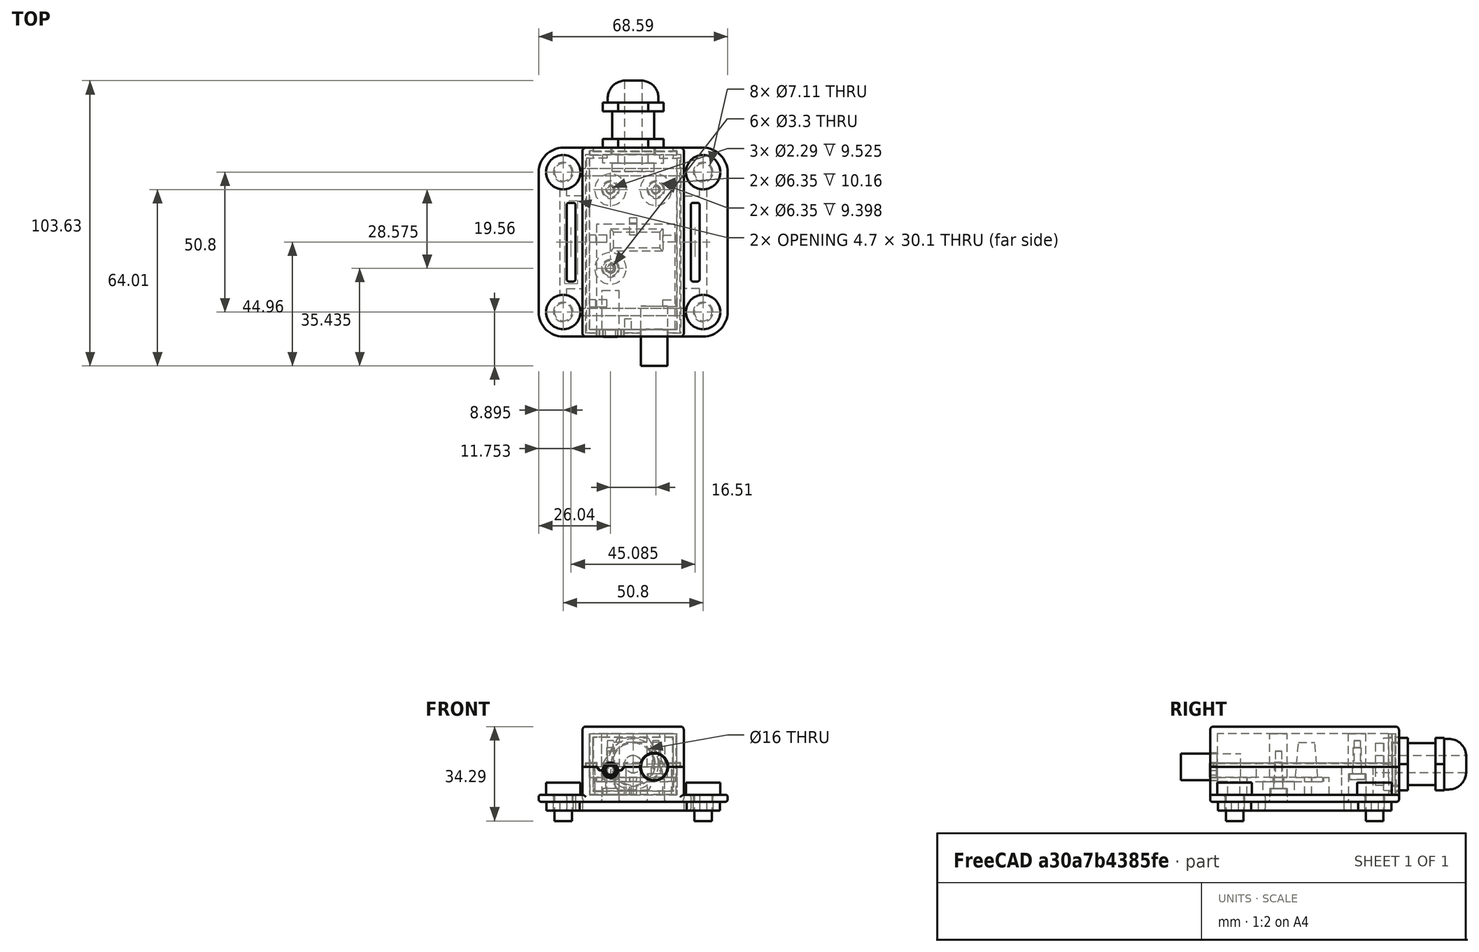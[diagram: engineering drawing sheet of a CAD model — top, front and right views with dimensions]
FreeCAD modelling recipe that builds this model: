
FCSTD DOCUMENT  (FreeCAD 0.20R29603 (Git))
Label: pump-box-v2-case
License: All rights reserved
LicenseURL: http://en.wikipedia.org/wiki/All_rights_reserved
objects: Sketcher::SketchObject×37, PartDesign::Body×22, PartDesign::Pad×20, PartDesign::FeatureBase×15, PartDesign::Pocket×14, App::DocumentObjectGroup×8, PartDesign::Fillet×6, Mesh::Feature×4, PartDesign::Revolution×3
note: 160 computed .brp shape members not serialized (recipe doc carries the construction recipe); baked Part::Feature solids carry a one-line shape summary decoded from their .brp

FEATURE [Sketcher::SketchObject] Sketch  label="pcb plan"
  FullyConstrained = true
  MapMode = 5
  Support = -> [XY_Plane]
  sketch-geometry (5):
    g0: LineSegment StartX=1.27 StartY=0 StartZ=0 EndX=29.845 EndY=0 EndZ=0
    g1: LineSegment StartX=29.845 StartY=0 StartZ=0 EndX=29.845 EndY=38.1 EndZ=0
    g2: LineSegment StartX=29.845 StartY=38.1 StartZ=0 EndX=1.27 EndY=38.1 EndZ=0
    g3: LineSegment StartX=1.27 StartY=38.1 StartZ=0 EndX=1.27 EndY=0 EndZ=0
    g4: Circle CenterX=6.35 CenterY=22.225 CenterZ=0 NormalX=0 NormalY=0 NormalZ=1 AngleXU=0 Radius=1.9304
  constraints (15):
    c: Coincident(g0,g1)
    c: Coincident(g1,g2)
    c: Coincident(g2,g3)
    c: Coincident(g3,g0)
    c: Horizontal(g0)
    c: Horizontal(g2)
    c: Vertical(g1)
    c: Vertical(g3)
    c: PointOnObject(g0,g-1)
    c: DistanceX(g-1,g0) = 1.27
    c: DistanceX(g0,g0) = 28.575
    c: DistanceY(g3,g3) = 38.1
    c: DistanceY(g4,g2) = 15.875
    c: DistanceX(g-1,g4) = 6.35
    c: Diameter(g4) = 3.8608
FEATURE [PartDesign::Pad] Pad  label="pcb slab"
  Direction = (0,0,1)
  Length = 1.5875
  Length2 = 10
  Profile = -> Sketch
  ReferenceAxis = -> Sketch [N_Axis]
  Reversed = true
  Type = 0
FEATURE [Sketcher::SketchObject] Sketch001  label="pcb terminal block plan"
  ExternalGeometry = -> [Pad]
  FullyConstrained = true
  MapMode = 5
  Support = -> [Pad]
  sketch-geometry (6):
    g0: LineSegment StartX=6.35 StartY=36.449 StartZ=0 EndX=25.4 EndY=36.449 EndZ=0
    g1: LineSegment StartX=25.4 StartY=36.449 StartZ=0 EndX=25.4 EndY=28.321 EndZ=0
    g2: LineSegment StartX=25.4 StartY=28.321 StartZ=0 EndX=6.35 EndY=28.321 EndZ=0
    g3: LineSegment StartX=6.35 StartY=28.321 StartZ=0 EndX=6.35 EndY=36.449 EndZ=0
    g4: LineSegment StartX=6.35 StartY=36.449 StartZ=0 EndX=15.875 EndY=32.385 EndZ=0
    g5: LineSegment StartX=15.875 StartY=32.385 StartZ=0 EndX=25.4 EndY=28.321 EndZ=0
  constraints (17):
    c: Coincident(g0,g1)
    c: Coincident(g1,g2)
    c: Coincident(g2,g3)
    c: Coincident(g3,g0)
    c: Horizontal(g0)
    c: Horizontal(g2)
    c: Vertical(g1)
    c: Vertical(g3)
    c: DistanceX(g0,g0) = 19.05
    c: DistanceY(g1,g1) = 8.128
    c: Coincident(g0,g4)
    c: Coincident(g4,g5)
    c: Coincident(g5,g1)
    c: Equal(g4,g5)
    c: Parallel(g4,g5)
    c: DistanceX(g-1,g4) = 15.875
    c: DistanceY(g4,g-3) = 5.715
FEATURE [PartDesign::Pad] Pad001  label="pcb with terminal block"
  BaseFeature = -> Pad
  Direction = (0,0,1)
  Length = 12.7
  Length2 = 10
  Profile = -> Sketch001
  ReferenceAxis = -> Sketch001 [N_Axis]
  TaperAngle = -5
  Type = 0
FEATURE [Sketcher::SketchObject] Sketch002  label="pcb audio block plan"
  FullyConstrained = true
  MapMode = 5
  Support = -> [Pad001]
  sketch-geometry (6):
    g0: LineSegment StartX=3.3528 StartY=14.1478 StartZ=0 EndX=9.3472 EndY=14.1478 EndZ=0
    g1: LineSegment StartX=9.3472 StartY=14.1478 StartZ=0 EndX=9.3472 EndY=-0.3302 EndZ=0
    g2: LineSegment StartX=9.3472 StartY=-0.3302 StartZ=0 EndX=3.3528 EndY=-0.3302 EndZ=0
    g3: LineSegment StartX=3.3528 StartY=-0.3302 StartZ=0 EndX=3.3528 EndY=14.1478 EndZ=0
    g4: LineSegment StartX=3.3528 StartY=14.1478 StartZ=0 EndX=6.35 EndY=6.9088 EndZ=0
    g5: LineSegment StartX=6.35 StartY=6.9088 StartZ=0 EndX=9.3472 EndY=-0.3302 EndZ=0
  constraints (17):
    c: Coincident(g0,g1)
    c: Coincident(g1,g2)
    c: Coincident(g2,g3)
    c: Coincident(g3,g0)
    c: Horizontal(g0)
    c: Horizontal(g2)
    c: Vertical(g1)
    c: Vertical(g3)
    c: DistanceY(g2,g-1) = 0.3302
    c: DistanceY(g3,g3) = 14.478
    c: DistanceX(g0,g0) = 5.9944
    c: Coincident(g0,g4)
    c: Coincident(g4,g5)
    c: Coincident(g5,g1)
    c: Equal(g5,g4)
    c: Parallel(g4,g5)
    c: DistanceX(g-1,g4) = 6.35
FEATURE [PartDesign::Pad] Pad002  label="pcb with audio block"
  BaseFeature = -> Pad001
  Direction = (0,0,1)
  Length = 5.08
  Length2 = 10
  Profile = -> Sketch002
  ReferenceAxis = -> Sketch002 [N_Axis]
  Type = 0
FEATURE [Sketcher::SketchObject] Sketch003  label="pcb audio sleeve plan"
  ExternalGeometry = -> [Pad002]
  FullyConstrained = true
  MapMode = 5
  Placement = pos=(0,-0.3302,0) rot=(1,0,0;1.5708rad)
  Support = -> [Pad002]
  sketch-geometry (4):
    g0: LineSegment StartX=3.3528 StartY=5.08 StartZ=0 EndX=6.35 EndY=2.54 EndZ=0
    g1: LineSegment StartX=6.35 StartY=2.54 StartZ=0 EndX=9.3472 EndY=0 EndZ=0
    g2: Circle CenterX=6.35 CenterY=2.54 CenterZ=0 NormalX=0 NormalY=0 NormalZ=1 AngleXU=0 Radius=2.5019
    g3: Circle CenterX=6.35 CenterY=2.54 CenterZ=0 NormalX=0 NormalY=0 NormalZ=1 AngleXU=0 Radius=1.7399
  constraints (9):
    c: Coincident(g0,g-3)
    c: Coincident(g0,g1)
    c: Coincident(g1,g-4)
    c: Parallel(g0,g1)
    c: Equal(g0,g1)
    c: Coincident(g2,g0)
    c: Coincident(g3,g2)
    c: Diameter(g3) = 3.4798
    c: Diameter(g2) = 5.0038
FEATURE [PartDesign::Pad] Pad003  label="pcb with audio sleeve"
  BaseFeature = -> Pad002
  Direction = (0,-1,2e-16)
  Length = 2.4892
  Length2 = 10
  Profile = -> Sketch003
  ReferenceAxis = -> Sketch003 [N_Axis]
  Type = 0
FEATURE [Sketcher::SketchObject] Sketch004  label="pcb bnc support plan"
  FullyConstrained = true
  MapMode = 5
  Support = -> [Pad003]
  sketch-geometry (6):
    g0: LineSegment StartX=17.399 StartY=8.4582 StartZ=0 EndX=27.051 EndY=8.4582 EndZ=0
    g1: LineSegment StartX=27.051 StartY=8.4582 StartZ=0 EndX=27.051 EndY=-0.3302 EndZ=0
    g2: LineSegment StartX=27.051 StartY=-0.3302 StartZ=0 EndX=17.399 EndY=-0.3302 EndZ=0
    g3: LineSegment StartX=17.399 StartY=-0.3302 StartZ=0 EndX=17.399 EndY=8.4582 EndZ=0
    g4: LineSegment StartX=17.399 StartY=8.4582 StartZ=0 EndX=22.225 EndY=4.064 EndZ=0
    g5: LineSegment StartX=22.225 StartY=4.064 StartZ=0 EndX=27.051 EndY=-0.3302 EndZ=0
  constraints (17):
    c: Coincident(g0,g1)
    c: Coincident(g1,g2)
    c: Coincident(g2,g3)
    c: Coincident(g3,g0)
    c: Horizontal(g0)
    c: Horizontal(g2)
    c: Vertical(g1)
    c: Vertical(g3)
    c: DistanceX(g0,g0) = 9.652
    c: DistanceY(g1,g1) = 8.7884
    c: Coincident(g0,g4)
    c: Coincident(g4,g5)
    c: Coincident(g5,g1)
    c: Parallel(g5,g4)
    c: Equal(g4,g5)
    c: DistanceX(g-1,g4) = 22.225
    c: DistanceY(g2,g-1) = 0.3302
FEATURE [PartDesign::Pad] Pad004  label="pcb with bnc support"
  BaseFeature = -> Pad003
  Direction = (0,0,1)
  Length = 3.7846
  Length2 = 10
  Profile = -> Sketch004
  ReferenceAxis = -> Sketch004 [N_Axis]
  Type = 0
FEATURE [Sketcher::SketchObject] Sketch005  label="pcb bnc tube plan"
  ExternalGeometry = -> [Pad004]
  FullyConstrained = true
  MapMode = 5
  Placement = pos=(0,8.4582,0) rot=(0,0.707107,0.707107;3.14159rad)
  Support = -> [Pad004]
  sketch-geometry (3):
    g0: LineSegment StartX=-17.399 StartY=3.7846 StartZ=0 EndX=-22.225 EndY=3.7846 EndZ=0
    g1: LineSegment StartX=-22.225 StartY=3.7846 StartZ=0 EndX=-27.051 EndY=3.7846 EndZ=0
    g2: Circle CenterX=-22.225 CenterY=3.7846 CenterZ=0 NormalX=0 NormalY=0 NormalZ=1 AngleXU=0 Radius=4.826
  constraints (7):
    c: Coincident(g-3,g0)
    c: Coincident(g0,g1)
    c: Coincident(g1,g-3)
    c: Coincident(g2,g0)
    c: PointOnObject(g1,g2)
    c: Equal(g1,g0)
    c: Horizontal(g1)
FEATURE [PartDesign::Pad] Pad005  label="pcb with bnc tube"
  BaseFeature = -> Pad004
  Direction = (0,1,-2e-16)
  Length = 21.7932
  Length2 = 10
  Profile = -> Sketch005
  ReferenceAxis = -> Sketch005 [N_Axis]
  Reversed = true
  Type = 0
FEATURE [PartDesign::Body] Body  label="pcb body"
  Group = -> [Sketch,Pad,Sketch001,Pad001,Sketch002,Pad002,Sketch003,Pad003,Sketch004,Pad004,Sketch005,Pad005]
  Origin = -> Origin
  Tip = -> Pad005
FEATURE [App::DocumentObjectGroup] Group001  label="pcb parts"
  Group = -> [Body]
FEATURE [Sketcher::SketchObject] Sketch006  label="cable gland profile"
  FullyConstrained = true
  MapMode = 5
  Placement = pos=(0,0,0) rot=(1,0,0;1.5708rad)
  Support = -> [XZ_Plane001]
  sketch-geometry (23):
    g0: LineSegment StartX=8.636 StartY=0 StartZ=0 EndX=8.636 EndY=7.62 EndZ=0
    g1: LineSegment StartX=8.636 StartY=7.62 StartZ=0 EndX=5.5626 EndY=7.62 EndZ=0
    g2: LineSegment StartX=5.5626 StartY=7.62 StartZ=0 EndX=5.5626 EndY=12.7 EndZ=0
    g3: LineSegment StartX=5.5626 StartY=12.7 StartZ=0 EndX=2.3876 EndY=12.7 EndZ=0
    g4: LineSegment StartX=2.3876 StartY=12.7 StartZ=0 EndX=2.3876 EndY=7.62 EndZ=0
    g5: LineSegment StartX=2.3876 StartY=7.62 StartZ=0 EndX=0 EndY=7.62 EndZ=0
    g6: LineSegment StartX=0 StartY=7.62 StartZ=0 EndX=0 EndY=12.7 EndZ=0
    g7: LineSegment StartX=0 StartY=12.7 StartZ=0 EndX=-3.175 EndY=12.7 EndZ=0
    g8: LineSegment StartX=-3.175 StartY=12.7 StartZ=0 EndX=-3.175 EndY=7.62 EndZ=0
    g9: LineSegment StartX=-3.175 StartY=7.62 StartZ=0 EndX=-13.2715 EndY=7.62 EndZ=0
    g10: LineSegment StartX=-13.2715 StartY=7.62 StartZ=0 EndX=-13.2715 EndY=12.7 EndZ=0
    g11: LineSegment StartX=-13.2715 StartY=12.7 StartZ=0 EndX=-16.4465 EndY=12.7 EndZ=0
    g12: LineSegment StartX=-16.4465 StartY=12.7 StartZ=0 EndX=-16.4465 EndY=9.2075 EndZ=0
    g13: LineSegment StartX=-16.4465 StartY=9.2075 StartZ=0 EndX=-18.034 EndY=9.2075 EndZ=0
    g14: LineSegment StartX=-18.034 StartY=9.2075 StartZ=0 EndX=-18.034 EndY=2.8575 EndZ=0
    g15: LineSegment StartX=-18.034 StartY=2.8575 StartZ=0 EndX=-24.384 EndY=2.8575 EndZ=0
    g16: LineSegment StartX=-24.384 StartY=2.8575 StartZ=0 EndX=-24.384 EndY=0 EndZ=0
    g17: LineSegment StartX=-24.384 StartY=0 StartZ=0 EndX=8.636 EndY=0 EndZ=0
    g18: ArcOfCircle CenterX=-18.034 CenterY=2.8575 CenterZ=0 NormalX=0 NormalY=0 NormalZ=1 AngleXU=0 Radius=6.35 StartAngle=1.5708 EndAngle=3.14159
    g19: LineSegment StartX=-3.175 StartY=7.62 StartZ=0 EndX=0 EndY=7.62 EndZ=0
    g20: LineSegment StartX=2.3876 StartY=7.62 StartZ=0 EndX=5.5626 EndY=7.62 EndZ=0
    g21: LineSegment StartX=2.3876 StartY=12.7 StartZ=0 EndX=0 EndY=12.7 EndZ=0
    g22: LineSegment StartX=-3.175 StartY=12.7 StartZ=0 EndX=-13.2715 EndY=12.7 EndZ=0
  constraints (64):
    c: PointOnObject(g0,g-1)
    c: Vertical(g0)
    c: Coincident(g0,g1)
    c: Horizontal(g1)
    c: Coincident(g1,g2)
    c: Vertical(g2)
    c: Coincident(g2,g3)
    c: Horizontal(g3)
    c: Coincident(g3,g4)
    c: Vertical(g4)
    c: Coincident(g4,g5)
    c: PointOnObject(g5,g-2)
    c: Horizontal(g5)
    c: Coincident(g5,g6)
    c: Coincident(g6,g7)
    c: Horizontal(g7)
    c: Coincident(g7,g8)
    c: Vertical(g8)
    c: Coincident(g8,g9)
    c: Horizontal(g9)
    c: Coincident(g9,g10)
    c: Vertical(g10)
    c: Coincident(g10,g11)
    c: Horizontal(g11)
    c: Coincident(g11,g12)
    c: Vertical(g12)
    c: Vertical(g6)
    c: Coincident(g12,g13)
    c: Horizontal(g13)
    c: Coincident(g13,g14)
    c: Vertical(g14)
    c: Coincident(g14,g15)
    c: Horizontal(g15)
    c: Coincident(g15,g16)
    c: Vertical(g16)
    c: Coincident(g16,g17)
    c: Coincident(g17,g0)
    c: Horizontal(g17)
    c: Coincident(g18,g14)
    c: Coincident(g18,g13)
    c: Coincident(g18,g16)
    c: Coincident(g19,g8)
    c: Coincident(g19,g5)
    c: Horizontal(g19)
    c: Coincident(g20,g4)
    c: Coincident(g20,g1)
    c: Horizontal(g20)
    c: Coincident(g21,g3)
    c: Coincident(g21,g6)
    c: Horizontal(g21)
    c: Coincident(g22,g7)
    c: Coincident(g22,g10)
    c: Horizontal(g22)
    c: DistanceY(g0,g0) = 7.62
    c: DistanceX(g-1,g0) = 8.636
    c: DistanceX(g17,g17) = 33.02
    c: Radius(g18) = 6.35
    c: DistanceY(g-1,g2) = 12.7
    c: DistanceY(g9,g12) = 1.5875
    c: DistanceX(g13,g11) = 1.5875
    c: Equal(g11,g7)
    c: Equal(g7,g3)
    c: DistanceX(g7,g7) = 3.175
    c: DistanceX(g21,g21) = 2.3876
FEATURE [PartDesign::Revolution] Revolution  label="cable gland revolved"
  Angle = 360
  Axis = (1,0,0)
  Base = (0,0,0)
  Placement = pos=(0,0,0) rot=(1,0,0;1.5708rad)
  Profile = -> Sketch006
  ReferenceAxis = -> Sketch006 [H_Axis]
FEATURE [Sketcher::SketchObject] Sketch007  label="cable gland hex plan"
  FullyConstrained = true
  MapMode = 5
  Placement = pos=(8.636,0,0) rot=(0.707107,0,0.707107;3.14159rad)
  Support = -> [Revolution]
  sketch-geometry (9):
    g0: LineSegment StartX=9.525 StartY=5.49926 StartZ=0 EndX=0 EndY=10.9985 EndZ=0
    g1: LineSegment StartX=0 StartY=10.9985 StartZ=0 EndX=-9.525 EndY=5.49926 EndZ=0
    g2: LineSegment StartX=-9.525 StartY=5.49926 StartZ=0 EndX=-9.525 EndY=-5.49926 EndZ=0
    g3: LineSegment StartX=-9.525 StartY=-5.49926 StartZ=0 EndX=0 EndY=-10.9985 EndZ=0
    g4: LineSegment StartX=0 StartY=-10.9985 StartZ=0 EndX=9.525 EndY=-5.49926 EndZ=0
    g5: LineSegment StartX=9.525 StartY=-5.49926 StartZ=0 EndX=9.525 EndY=5.49926 EndZ=0
    g6: Circle CenterX=0 CenterY=0 CenterZ=0 NormalX=0 NormalY=0 NormalZ=1 AngleXU=0 Radius=10.9985
    g7: Circle CenterX=0 CenterY=0 CenterZ=0 NormalX=0 NormalY=0 NormalZ=1 AngleXU=0 Radius=25.4
    g8: Circle CenterX=0 CenterY=0 CenterZ=0 NormalX=0 NormalY=0 NormalZ=1 AngleXU=0 Radius=3.175
  constraints (20):
    c: Coincident(g0,g1)
    c: Coincident(g1,g2)
    c: Coincident(g2,g3)
    c: Coincident(g3,g4)
    c: Coincident(g4,g5)
    c: Coincident(g5,g0)
    c: Equal(g0, g1-g5) x5
    c: PointOnObject(g0,g6)
    c: PointOnObject(g1,g6)
    c: PointOnObject(g2,g6)
    c: PointOnObject(g3,g6)
    c: PointOnObject(g4,g6)
    c: PointOnObject(g5,g6)
    c: Coincident(g6,g-1)
    c: Coincident(g7,g6)
    c: Diameter(g7) = 50.8
    c: Coincident(g8,g7)
    c: PointOnObject(g0,g-2)
    c: DistanceX(g2,g4) = 19.05
    c: Diameter(g8) = 6.35
FEATURE [PartDesign::Pocket] Pocket  label="cable gland with hex"
  BaseFeature = -> Revolution
  Direction = (-1,0,2e-16)
  Length = 5
  Length2 = 5
  Placement = pos=(0,0,0) rot=(1,0,0;1.5708rad)
  Profile = -> Sketch007
  ReferenceAxis = -> Sketch007 [N_Axis]
  Type = 1
FEATURE [PartDesign::Body] Body001  label="cable gland body"
  Group = -> [Sketch006,Revolution,Sketch007,Pocket]
  Origin = -> Origin001
  Tip = -> Pocket
FEATURE [App::DocumentObjectGroup] Group004  label="cable gland parts"
  Group = -> [Body001]
FEATURE [PartDesign::FeatureBase] Clone
  BaseFeature = -> Body
FEATURE [PartDesign::Body] Body002  label="pcb clone for mockup"
  BaseFeature = -> Body
  Group = -> [Clone]
  Origin = -> Origin002
  Placement = pos=(1.27,0.127,0) rot=(0,0,1;0rad)
  Tip = -> Clone
FEATURE [PartDesign::FeatureBase] Clone001
  BaseFeature = -> Body001
FEATURE [PartDesign::Body] Body003  label="cable gland clone for mockup"
  BaseFeature = -> Body001
  Group = -> [Clone001]
  Origin = -> Origin003
  Placement = pos=(15.875,66.04,4.7625) rot=(0,0,-1;1.5708rad)
  Tip = -> Clone001
FEATURE [Sketcher::SketchObject] Sketch008  label="case mockup bottom footprint"
  FullyConstrained = true
  MapMode = 5
  Support = -> [XY_Plane004]
  sketch-geometry (8):
    g0: LineSegment StartX=-2.54 StartY=-2.54 StartZ=0 EndX=34.29 EndY=-2.54 EndZ=0
    g1: LineSegment StartX=34.29 StartY=-2.54 StartZ=0 EndX=34.29 EndY=66.04 EndZ=0
    g2: LineSegment StartX=34.29 StartY=66.04 StartZ=0 EndX=-2.54 EndY=66.04 EndZ=0
    g3: LineSegment StartX=-2.54 StartY=66.04 StartZ=0 EndX=-2.54 EndY=-2.54 EndZ=0
    g4: LineSegment StartX=31.75 StartY=66.04 StartZ=0 EndX=31.75 EndY=63.5 EndZ=0
    g5: LineSegment StartX=31.75 StartY=63.5 StartZ=0 EndX=34.29 EndY=63.5 EndZ=0
    g6: LineSegment StartX=-2.54 StartY=1e-16 StartZ=0 EndX=0 EndY=1e-16 EndZ=0
    g7: LineSegment StartX=0 StartY=1e-16 StartZ=0 EndX=0 EndY=-2.54 EndZ=0
  constraints (25):
    c: Coincident(g0,g1)
    c: Coincident(g1,g2)
    c: Coincident(g2,g3)
    c: Coincident(g3,g0)
    c: Horizontal(g0)
    c: Horizontal(g2)
    c: Vertical(g1)
    c: Vertical(g3)
    c: PointOnObject(g4,g2)
    c: Vertical(g4)
    c: PointOnObject(g5,g1)
    c: Horizontal(g5)
    c: PointOnObject(g6,g3)
    c: Horizontal(g6)
    c: PointOnObject(g7,g0)
    c: Vertical(g7)
    c: Equal(g6,g7)
    c: Equal(g7,g4)
    c: Equal(g4,g5)
    c: DistanceY(g0,g6) = 2.54
    c: DistanceY(g6,g4) = 63.5
    c: DistanceX(g6,g4) = 31.75
    c: Coincident(g4,g5)
    c: Coincident(g6,g7)
    c: Coincident(g6,g-1)
FEATURE [PartDesign::Pad] Pad006  label="case mockup bottom block"
  Direction = (0,0,1)
  Length = 8.89
  Length2 = 10
  Profile = -> Sketch008
  ReferenceAxis = -> Sketch008 [N_Axis]
  Reversed = true
  Type = 0
FEATURE [Sketcher::SketchObject] Sketch009  label="case mockup bottom pocket plan"
  FullyConstrained = true
  MapMode = 5
  Support = -> [Pad006]
  sketch-geometry (4):
    g0: LineSegment StartX=0 StartY=0 StartZ=0 EndX=31.75 EndY=0 EndZ=0
    g1: LineSegment StartX=31.75 StartY=0 StartZ=0 EndX=31.75 EndY=62.23 EndZ=0
    g2: LineSegment StartX=31.75 StartY=62.23 StartZ=0 EndX=0 EndY=62.23 EndZ=0
    g3: LineSegment StartX=0 StartY=62.23 StartZ=0 EndX=0 EndY=0 EndZ=0
  constraints (11):
    c: Coincident(g0,g1)
    c: Coincident(g1,g2)
    c: Coincident(g2,g3)
    c: Coincident(g3,g0)
    c: Horizontal(g0)
    c: Horizontal(g2)
    c: Vertical(g1)
    c: Vertical(g3)
    c: Coincident(g0,g-1)
    c: DistanceY(g1,g1) = 62.23
    c: DistanceX(g2,g2) = 31.75
FEATURE [PartDesign::Pocket] Pocket001  label="case mockup bottom with pocket"
  BaseFeature = -> Pad006
  Direction = (0,0,-1)
  Length = 6.35
  Length2 = 5
  Profile = -> Sketch009
  ReferenceAxis = -> Sketch009 [N_Axis]
  Type = 0
FEATURE [Sketcher::SketchObject] Sketch010  label="case mockup bottom post plan"
  ExternalGeometry = -> [Pocket001]
  FullyConstrained = true
  MapMode = 5
  Placement = pos=(0,0,-6.35) rot=(0,0,1;0rad)
  Support = -> [Pocket001]
  sketch-geometry (34):
    g0: LineSegment StartX=0 StartY=31.75 StartZ=0 EndX=6.35 EndY=31.75 EndZ=0
    g1: LineSegment StartX=6.35 StartY=31.75 StartZ=0 EndX=6.35 EndY=34.29 EndZ=0
    g2: LineSegment StartX=6.35 StartY=34.29 StartZ=0 EndX=0 EndY=34.29 EndZ=0
    g3: LineSegment StartX=0 StartY=34.29 StartZ=0 EndX=0 EndY=31.75 EndZ=0
    g4: LineSegment StartX=31.75 StartY=31.75 StartZ=0 EndX=26.67 EndY=31.75 EndZ=0
    g5: LineSegment StartX=26.67 StartY=31.75 StartZ=0 EndX=26.67 EndY=34.29 EndZ=0
    g6: LineSegment StartX=26.67 StartY=34.29 StartZ=0 EndX=31.75 EndY=34.29 EndZ=0
    g7: LineSegment StartX=31.75 StartY=34.29 StartZ=0 EndX=31.75 EndY=31.75 EndZ=0
    g8: LineSegment StartX=0 StartY=8.255 StartZ=0 EndX=6.35 EndY=8.255 EndZ=0
    g9: LineSegment StartX=6.35 StartY=8.255 StartZ=0 EndX=6.35 EndY=10.795 EndZ=0
    g10: LineSegment StartX=6.35 StartY=10.795 StartZ=0 EndX=0 EndY=10.795 EndZ=0
    g11: LineSegment StartX=0 StartY=10.795 StartZ=0 EndX=0 EndY=8.255 EndZ=0
    g12: LineSegment StartX=31.75 StartY=8.255 StartZ=0 EndX=26.67 EndY=8.255 EndZ=0
    g13: LineSegment StartX=26.67 StartY=8.255 StartZ=0 EndX=26.67 EndY=10.795 EndZ=0
    g14: LineSegment StartX=26.67 StartY=10.795 StartZ=0 EndX=31.75 EndY=10.795 EndZ=0
    g15: LineSegment StartX=31.75 StartY=10.795 StartZ=0 EndX=31.75 EndY=8.255 EndZ=0
    g16: LineSegment StartX=14.605 StartY=40.64 StartZ=0 EndX=17.145 EndY=40.64 EndZ=0
    g17: LineSegment StartX=17.145 StartY=40.64 StartZ=0 EndX=17.145 EndY=34.29 EndZ=0
    g18: LineSegment StartX=17.145 StartY=34.29 StartZ=0 EndX=14.605 EndY=34.29 EndZ=0
    g19: LineSegment StartX=14.605 StartY=34.29 StartZ=0 EndX=14.605 EndY=40.64 EndZ=0
    g20: LineSegment StartX=12.7 StartY=0 StartZ=0 EndX=15.24 EndY=0 EndZ=0
    g21: LineSegment StartX=15.24 StartY=0 StartZ=0 EndX=15.24 EndY=3.81 EndZ=0
    g22: LineSegment StartX=15.24 StartY=3.81 StartZ=0 EndX=12.7 EndY=3.81 EndZ=0
    g23: LineSegment StartX=12.7 StartY=3.81 StartZ=0 EndX=12.7 EndY=0 EndZ=0
    g24: LineSegment StartX=6.35 StartY=31.75 StartZ=0 EndX=26.67 EndY=31.75 EndZ=0
    g25: LineSegment StartX=6.35 StartY=8.255 StartZ=0 EndX=26.67 EndY=8.255 EndZ=0
    g26: LineSegment StartX=14.605 StartY=34.29 StartZ=0 EndX=15.875 EndY=38.1 EndZ=0
    g27: LineSegment StartX=15.875 StartY=38.1 StartZ=0 EndX=17.145 EndY=34.29 EndZ=0
    g28: LineSegment StartX=7.62 StartY=50.8 StartZ=0 EndX=24.13 EndY=50.8 EndZ=0
    g29: Circle CenterX=7.62 CenterY=22.225 CenterZ=0 NormalX=0 NormalY=0 NormalZ=1 AngleXU=0 Radius=5.715
    g30: LineSegment StartX=7.62 StartY=50.8 StartZ=0 EndX=0 EndY=50.8 EndZ=0
    g31: LineSegment StartX=24.13 StartY=50.8 StartZ=0 EndX=31.75 EndY=50.8 EndZ=0
    g32: Circle CenterX=7.62 CenterY=50.8 CenterZ=0 NormalX=0 NormalY=0 NormalZ=1 AngleXU=0 Radius=5.715
    g33: Circle CenterX=24.13 CenterY=50.8 CenterZ=0 NormalX=0 NormalY=0 NormalZ=1 AngleXU=0 Radius=5.715
  constraints (98):
    c: Coincident(g0,g1)
    c: Coincident(g1,g2)
    c: Coincident(g2,g3)
    c: Coincident(g3,g0)
    c: Horizontal(g0)
    c: Horizontal(g2)
    c: Vertical(g1)
    c: Vertical(g3)
    c: PointOnObject(g0,g-2)
    c: Coincident(g4,g5)
    c: Coincident(g5,g6)
    c: Coincident(g6,g7)
    c: Coincident(g7,g4)
    c: Horizontal(g4)
    c: Horizontal(g6)
    c: Vertical(g5)
    c: Vertical(g7)
    c: Coincident(g8,g9)
    c: Coincident(g9,g10)
    c: Coincident(g10,g11)
    c: Coincident(g11,g8)
    c: Horizontal(g8)
    c: Horizontal(g10)
    c: Vertical(g9)
    c: Vertical(g11)
    c: PointOnObject(g8,g-2)
    c: Coincident(g12,g13)
    c: Coincident(g13,g14)
    c: Coincident(g14,g15)
    c: Coincident(g15,g12)
    c: Horizontal(g12)
    c: Horizontal(g14)
    c: Vertical(g13)
    c: Vertical(g15)
    c: Coincident(g16,g17)
    c: Coincident(g17,g18)
    c: Coincident(g18,g19)
    c: Coincident(g19,g16)
    c: Horizontal(g16)
    c: Horizontal(g18)
    c: Vertical(g17)
    c: Vertical(g19)
    c: Coincident(g20,g21)
    c: Coincident(g21,g22)
    c: Coincident(g22,g23)
    c: Coincident(g23,g20)
    c: Horizontal(g20)
    c: Horizontal(g22)
    c: Vertical(g21)
    c: Vertical(g23)
    c: PointOnObject(g20,g-1)
    c: PointOnObject(g6,g-3)
    c: PointOnObject(g14,g-3)
    c: DistanceX(g-1,g20) = 12.7
    c: DistanceY(g-1,g8) = 8.255
    c: Equal(g1,g18)
    c: Equal(g18,g5)
    c: Equal(g5,g13)
    c: Equal(g13,g9)
    c: DistanceY(g-1,g0) = 31.75
    c: Coincident(g24,g0)
    c: Coincident(g24,g4)
    c: Horizontal(g24)
    c: Coincident(g25,g8)
    c: Coincident(g25,g12)
    c: Horizontal(g25)
    c: DistanceY(g15,g15) = 2.54
    c: Coincident(g18,g26)
    c: Coincident(g26,g27)
    c: Coincident(g27,g17)
    c: Equal(g27,g26)
    c: DistanceX(g-1,g26) = 15.875
    c: DistanceY(g-3,g26) = 38.1
    c: DistanceY(g17,g26) = 3.81
    c: DistanceY(g26,g16) = 2.54
    c: DistanceX(g12,g12) = 5.08
    c: DistanceX(g8,g8) = 6.35
    c: Equal(g10,g2)
    c: Equal(g4,g14)
    c: DistanceY(g21,g21) = 3.81
    c: Equal(g13,g22)
    c: Horizontal(g28)
    c: Diameter(g29) = 11.43
    c: DistanceY(g-1,g29) = 22.225
    c: DistanceX(g-1,g29) = 7.62
    c: Coincident(g30,g28)
    c: PointOnObject(g30,g-2)
    c: Horizontal(g30)
    c: Coincident(g31,g28)
    c: PointOnObject(g31,g-3)
    c: Horizontal(g31)
    c: Equal(g31,g30)
    c: DistanceY(g-1,g28) = 50.8
    c: Coincident(g32,g28)
    c: Coincident(g33,g28)
    c: Equal(g32,g33)
    c: Equal(g33,g29)
    c: DistanceX(g31,g31) = 7.62
FEATURE [PartDesign::Pad] Pad007  label="case mockup bottom with posts"
  BaseFeature = -> Pocket001
  Direction = (0,0,1)
  Length = 6.35
  Length2 = 10
  Profile = -> Sketch010
  ReferenceAxis = -> Sketch010 [N_Axis]
  Type = 0
FEATURE [Sketcher::SketchObject] Sketch011  label="case mockup bottom board plan"
  ExternalGeometry = -> [Pad007]
  FullyConstrained = true
  MapMode = 5
  Support = -> [Pad007]
  sketch-geometry (7):
    g0: LineSegment StartX=2.286 StartY=0 StartZ=0 EndX=31.369 EndY=0 EndZ=0
    g1: LineSegment StartX=31.369 StartY=0 StartZ=0 EndX=31.369 EndY=38.608 EndZ=0
    g2: LineSegment StartX=31.369 StartY=38.608 StartZ=0 EndX=2.286 EndY=38.608 EndZ=0
    g3: LineSegment StartX=2.286 StartY=38.608 StartZ=0 EndX=2.286 EndY=0 EndZ=0
    g4: LineSegment StartX=2.286 StartY=38.608 StartZ=0 EndX=2.286 EndY=25.6704 EndZ=0
    g5: LineSegment StartX=2.286 StartY=0 StartZ=0 EndX=2.286 EndY=18.7796 EndZ=0
    g6: ArcOfCircle CenterX=7.62 CenterY=22.225 CenterZ=0 NormalX=0 NormalY=0 NormalZ=1 AngleXU=0 Radius=6.35 StartAngle=2.56808 EndAngle=3.71511
  constraints (20):
    c: Coincident(g0,g1)
    c: Coincident(g1,g2)
    c: Horizontal(g0)
    c: Horizontal(g2)
    c: Vertical(g1)
    c: PointOnObject(g0,g-1)
    c: DistanceY(g1,g1) = 38.608
    c: DistanceX(g2,g2) = 29.083
    c: DistanceX(g-1,g0) = 2.286
    c: Coincident(g3,g0)
    c: Vertical(g3)
    c: Coincident(g3,g2)
    c: Coincident(g2,g4)
    c: Coincident(g5,g0)
    c: Coincident(g6,g-3)
    c: Coincident(g6,g4)
    c: Coincident(g6,g5)
    c: Vertical(g5)
    c: Vertical(g4)
    c: Diameter(g6) = 12.7
FEATURE [PartDesign::Pocket] Pocket002  label="case mockup bottom with board cutout"
  BaseFeature = -> Pad007
  Direction = (0,0,-1)
  Length = 1.5875
  Length2 = 5
  Profile = -> Sketch011
  ReferenceAxis = -> Sketch011 [N_Axis]
  Type = 0
FEATURE [Sketcher::SketchObject] Sketch012  label="case mockup bottom extension plan"
  ExternalGeometry = -> [Pocket002]
  FullyConstrained = true
  MapMode = 5
  Support = -> [Pocket002]
  sketch-geometry (10):
    g0: LineSegment StartX=-2.54 StartY=66.04 StartZ=0 EndX=34.29 EndY=66.04 EndZ=0
    g1: LineSegment StartX=34.29 StartY=66.04 StartZ=0 EndX=34.29 EndY=-2.54 EndZ=0
    g2: LineSegment StartX=34.29 StartY=-2.54 StartZ=0 EndX=-2.54 EndY=-2.54 EndZ=0
    g3: LineSegment StartX=-2.54 StartY=-2.54 StartZ=0 EndX=-2.54 EndY=66.04 EndZ=0
    g4: LineSegment StartX=31.75 StartY=0 StartZ=0 EndX=0 EndY=0 EndZ=0
    g5: LineSegment StartX=0 StartY=0 StartZ=0 EndX=0 EndY=62.23 EndZ=0
    g6: LineSegment StartX=0 StartY=62.23 StartZ=0 EndX=31.75 EndY=62.23 EndZ=0
    g7: LineSegment StartX=31.75 StartY=62.23 StartZ=0 EndX=31.75 EndY=0 EndZ=0
    g8: Circle CenterX=7.62 CenterY=50.8 CenterZ=0 NormalX=0 NormalY=0 NormalZ=1 AngleXU=0 Radius=5.715
    g9: Circle CenterX=24.13 CenterY=50.8 CenterZ=0 NormalX=0 NormalY=0 NormalZ=1 AngleXU=0 Radius=5.715
  constraints (24):
    c: Coincident(g0,g1)
    c: Coincident(g1,g2)
    c: Coincident(g2,g3)
    c: Coincident(g3,g0)
    c: Horizontal(g0)
    c: Horizontal(g2)
    c: Vertical(g1)
    c: Vertical(g3)
    c: Coincident(g0,g-3)
    c: Coincident(g1,g-4)
    c: Coincident(g4,g5)
    c: Coincident(g5,g6)
    c: Coincident(g6,g7)
    c: Coincident(g7,g4)
    c: Horizontal(g4)
    c: Horizontal(g6)
    c: Vertical(g5)
    c: Vertical(g7)
    c: Coincident(g4,g-6)
    c: Coincident(g5,g-5)
    c: Coincident(g8,g-7)
    c: Coincident(g9,g-8)
    c: Equal(g-7,g8)
    c: Equal(g8,g9)
FEATURE [PartDesign::Pad] Pad008  label="case mockup bottom with extension"
  BaseFeature = -> Pocket002
  Direction = (0,0,1)
  Length = 3.81
  Length2 = 10
  Profile = -> Sketch012
  ReferenceAxis = -> Sketch012 [N_Axis]
  Type = 0
FEATURE [Sketcher::SketchObject] Sketch013  label="case mockup bottom front cutout profile"
  ExternalGeometry = -> [Pad008]
  FullyConstrained = true
  MapMode = 5
  Placement = pos=(0,-2.54,0) rot=(1,0,0;1.5708rad)
  Support = -> [Pad008]
  sketch-geometry (8):
    g0: Circle CenterX=23.495 CenterY=3.81 CenterZ=0 NormalX=0 NormalY=0 NormalZ=1 AngleXU=0 Radius=5.08
    g1: LineSegment StartX=2.54 StartY=3.81 StartZ=0 EndX=3.556 EndY=2.54 EndZ=0
    g2: LineSegment StartX=3.556 StartY=2.54 StartZ=0 EndX=4.826 EndY=2.54 EndZ=0
    g3: LineSegment StartX=4.826 StartY=2.54 StartZ=0 EndX=10.414 EndY=2.54 EndZ=0
    g4: LineSegment StartX=10.414 StartY=2.54 StartZ=0 EndX=11.684 EndY=2.54 EndZ=0
    g5: LineSegment StartX=11.684 StartY=2.54 StartZ=0 EndX=12.7 EndY=3.81 EndZ=0
    g6: LineSegment StartX=12.7 StartY=3.81 StartZ=0 EndX=2.54 EndY=3.81 EndZ=0
    g7: ArcOfCircle CenterX=7.62 CenterY=2.54 CenterZ=0 NormalX=0 NormalY=0 NormalZ=1 AngleXU=0 Radius=2.794 StartAngle=3.14159 EndAngle=6.28319
  constraints (24):
    c: Coincident(g1,g2)
    c: Coincident(g2,g3)
    c: Horizontal(g3)
    c: Coincident(g3,g4)
    c: Horizontal(g4)
    c: Coincident(g4,g5)
    c: Coincident(g5,g6)
    c: Coincident(g6,g1)
    c: Horizontal(g6)
    c: Horizontal(g2)
    c: PointOnObject(g7,g3)
    c: Coincident(g7,g2)
    c: Coincident(g7,g4)
    c: DistanceY(g-1,g7) = 2.54
    c: PointOnObject(g1,g-3)
    c: PointOnObject(g0,g-3)
    c: DistanceX(g-1,g7) = 7.62
    c: DistanceX(g-1,g0) = 23.495
    c: Diameter(g7) = 5.588
    c: Diameter(g0) = 10.16
    c: Equal(g2,g4)
    c: DistanceX(g1,g7) = 4.064
    c: Equal(g5,g1)
    c: DistanceX(g7,g5) = 5.08
FEATURE [PartDesign::Pocket] Pocket003  label="case mockup bottom with front cutout"
  BaseFeature = -> Pad008
  Direction = (0,1,-2e-16)
  Length = 5.08
  Length2 = 5
  Profile = -> Sketch013
  ReferenceAxis = -> Sketch013 [N_Axis]
  Type = 0
FEATURE [Sketcher::SketchObject] Sketch014  label="case mockup bottom hole plan"
  ExternalGeometry = -> [Pocket003]
  FullyConstrained = true
  MapMode = 5
  Placement = pos=(0,0,3.81) rot=(0,0,1;0rad)
  Support = -> [Pocket003]
  sketch-geometry (3):
    g0: Circle CenterX=7.62 CenterY=50.8 CenterZ=0 NormalX=0 NormalY=0 NormalZ=1 AngleXU=0 Radius=1.651
    g1: Circle CenterX=24.13 CenterY=50.8 CenterZ=0 NormalX=0 NormalY=0 NormalZ=1 AngleXU=0 Radius=1.651
    g2: Circle CenterX=7.62 CenterY=22.225 CenterZ=0 NormalX=0 NormalY=0 NormalZ=1 AngleXU=0 Radius=1.651
  constraints (6):
    c: Coincident(g0,g-3)
    c: Coincident(g1,g-4)
    c: Coincident(g2,g-5)
    c: Equal(g0,g1)
    c: Equal(g0,g2)
    c: Diameter(g0) = 3.302
FEATURE [PartDesign::Pocket] Pocket004  label="case mockup bottom with holes"
  BaseFeature = -> Pocket003
  Direction = (0,0,-1)
  Length = 5
  Length2 = 5
  Profile = -> Sketch014
  ReferenceAxis = -> Sketch014 [N_Axis]
  Type = 1
FEATURE [Sketcher::SketchObject] Sketch015  label="case mockup bottom deep hole plan"
  ExternalGeometry = -> [Pocket004]
  FullyConstrained = true
  MapMode = 5
  Placement = pos=(0,0,-8.89) rot=(1,0,0;3.14159rad)
  Support = -> [Pocket004]
  sketch-geometry (2):
    g0: Circle CenterX=7.62 CenterY=-50.8 CenterZ=0 NormalX=0 NormalY=0 NormalZ=1 AngleXU=0 Radius=3.175
    g1: Circle CenterX=24.13 CenterY=-50.8 CenterZ=0 NormalX=0 NormalY=0 NormalZ=1 AngleXU=0 Radius=3.175
  constraints (4):
    c: Coincident(g0,g-3)
    c: Coincident(g1,g-4)
    c: Equal(g0,g1)
    c: Diameter(g0) = 6.35
FEATURE [PartDesign::Pocket] Pocket005  label="case mockup bottom with deep holes"
  BaseFeature = -> Pocket004
  Direction = (0,0,1)
  Length = 10.16
  Length2 = 5
  Profile = -> Sketch015
  ReferenceAxis = -> Sketch015 [N_Axis]
  Type = 0
FEATURE [Sketcher::SketchObject] Sketch016  label="case mockup bottom shallow hole plan"
  ExternalGeometry = -> [Pocket005]
  FullyConstrained = true
  MapMode = 5
  Placement = pos=(0,0,-8.89) rot=(1,0,0;3.14159rad)
  Support = -> [Pocket005]
  sketch-geometry (1):
    g0: Circle CenterX=7.62 CenterY=-22.225 CenterZ=0 NormalX=0 NormalY=0 NormalZ=1 AngleXU=0 Radius=3.175
  constraints (2):
    c: Coincident(g0,g-3)
    c: Diameter(g0) = 6.35
FEATURE [PartDesign::Pocket] Pocket006  label="case mockup bottom with shallow hole"
  BaseFeature = -> Pocket005
  Direction = (0,0,1)
  Length = 4.7625
  Length2 = 5
  Profile = -> Sketch016
  ReferenceAxis = -> Sketch016 [N_Axis]
  Type = 0
FEATURE [Sketcher::SketchObject] Sketch017  label="case mockup bottom lip plan"
  ExternalGeometry = -> [Pocket006]
  FullyConstrained = true
  MapMode = 5
  Placement = pos=(0,0,3.81) rot=(0,0,1;0rad)
  Support = -> [Pocket006]
  sketch-geometry (19):
    g0: LineSegment StartX=0 StartY=62.23 StartZ=0 EndX=-1.143 EndY=62.23 EndZ=0
    g1: LineSegment StartX=-1.143 StartY=62.23 StartZ=0 EndX=-1.143 EndY=-1.143 EndZ=0
    g2: LineSegment StartX=-1.143 StartY=-1.143 StartZ=0 EndX=2.54 EndY=-1.143 EndZ=0
    g3: LineSegment StartX=2.54 StartY=-1.143 StartZ=0 EndX=2.54 EndY=0 EndZ=0
    g4: LineSegment StartX=2.54 StartY=0 StartZ=0 EndX=0 EndY=0 EndZ=0
    g5: LineSegment StartX=0 StartY=0 StartZ=0 EndX=0 EndY=62.23 EndZ=0
    g6: LineSegment StartX=0 StartY=62.23 StartZ=0 EndX=31.75 EndY=62.23 EndZ=0
    g7: LineSegment StartX=31.75 StartY=62.23 StartZ=0 EndX=31.75 EndY=0 EndZ=0
    g8: LineSegment StartX=31.75 StartY=0 StartZ=0 EndX=28.575 EndY=0 EndZ=0
    g9: LineSegment StartX=28.575 StartY=0 StartZ=0 EndX=28.575 EndY=-1.143 EndZ=0
    g10: LineSegment StartX=28.575 StartY=-1.143 StartZ=0 EndX=32.893 EndY=-1.143 EndZ=0
    g11: LineSegment StartX=32.893 StartY=-1.143 StartZ=0 EndX=32.893 EndY=62.23 EndZ=0
    g12: LineSegment StartX=32.893 StartY=62.23 StartZ=0 EndX=31.75 EndY=62.23 EndZ=0
    g13: LineSegment StartX=2.54 StartY=0 StartZ=0 EndX=12.7 EndY=0 EndZ=0
    g14: LineSegment StartX=12.7 StartY=0 StartZ=0 EndX=12.7 EndY=-1.143 EndZ=0
    g15: LineSegment StartX=12.7 StartY=-1.143 StartZ=0 EndX=18.415 EndY=-1.143 EndZ=0
    g16: LineSegment StartX=18.415 StartY=-1.143 StartZ=0 EndX=18.415 EndY=0 EndZ=0
    g17: LineSegment StartX=18.415 StartY=0 StartZ=0 EndX=12.7 EndY=0 EndZ=0
    g18: LineSegment StartX=18.415 StartY=0 StartZ=0 EndX=28.575 EndY=0 EndZ=0
  constraints (52):
    c: Coincident(g0,g1)
    c: Vertical(g1)
    c: Coincident(g1,g2)
    c: Horizontal(g2)
    c: Coincident(g2,g3)
    c: Vertical(g3)
    c: Coincident(g3,g4)
    c: Horizontal(g4)
    c: Coincident(g4,g5)
    c: Coincident(g5,g0)
    c: Vertical(g5)
    c: Coincident(g0,g6)
    c: Horizontal(g6)
    c: Coincident(g6,g7)
    c: Vertical(g7)
    c: Coincident(g7,g8)
    c: Horizontal(g8)
    c: Coincident(g8,g9)
    c: Coincident(g9,g10)
    c: Horizontal(g10)
    c: Coincident(g10,g11)
    c: Vertical(g11)
    c: Coincident(g11,g12)
    c: Coincident(g12,g6)
    c: Horizontal(g12)
    c: Horizontal(g0)
    c: Vertical(g9)
    c: Equal(g9,g3)
    c: Equal(g3,g0)
    c: Equal(g0,g12)
    c: Coincident(g3,g13)
    c: Horizontal(g13)
    c: Coincident(g13,g14)
    c: Vertical(g14)
    c: Coincident(g14,g15)
    c: Horizontal(g15)
    c: Coincident(g15,g16)
    c: Vertical(g16)
    c: Coincident(g16,g17)
    c: Coincident(g17,g13)
    c: Coincident(g16,g18)
    c: Coincident(g18,g8)
    c: Horizontal(g18)
    c: Horizontal(g17)
    c: Equal(g16,g9)
    c: DistanceX(g12,g12) = 1.143
    c: Coincident(g7,g-4)
    c: Coincident(g0,g-3)
    c: PointOnObject(g9,g-8)
    c: PointOnObject(g15,g-7)
    c: PointOnObject(g14,g-6)
    c: PointOnObject(g2,g-5)
FEATURE [PartDesign::Pad] Pad009  label="case mockup bottom with lip"
  BaseFeature = -> Pocket006
  Direction = (0,0,1)
  Length = 1.27
  Length2 = 10
  Profile = -> Sketch017
  ReferenceAxis = -> Sketch017 [N_Axis]
  Type = 0
FEATURE [Sketcher::SketchObject] Sketch018  label="case mockup bottom rear guide plan"
  ExternalGeometry = -> [Pad009]
  FullyConstrained = true
  MapMode = 5
  Placement = pos=(0,0,3.81) rot=(0,0,1;0rad)
  Support = -> [Pad009]
  sketch-geometry (13):
    g0: LineSegment StartX=1.27 StartY=66.04 StartZ=0 EndX=1.27 EndY=64.897 EndZ=0
    g1: LineSegment StartX=1.27 StartY=64.897 StartZ=0 EndX=0 EndY=64.897 EndZ=0
    g2: LineSegment StartX=0 StartY=64.897 StartZ=0 EndX=0 EndY=63.373 EndZ=0
    g3: LineSegment StartX=0 StartY=63.373 StartZ=0 EndX=1.27 EndY=63.373 EndZ=0
    g4: LineSegment StartX=1.27 StartY=63.373 StartZ=0 EndX=1.27 EndY=62.23 EndZ=0
    g5: LineSegment StartX=1.27 StartY=62.23 StartZ=0 EndX=30.48 EndY=62.23 EndZ=0
    g6: LineSegment StartX=30.48 StartY=62.23 StartZ=0 EndX=30.48 EndY=63.373 EndZ=0
    g7: LineSegment StartX=30.48 StartY=63.373 StartZ=0 EndX=31.75 EndY=63.373 EndZ=0
    g8: LineSegment StartX=31.75 StartY=63.373 StartZ=0 EndX=31.75 EndY=64.897 EndZ=0
    g9: LineSegment StartX=31.75 StartY=64.897 StartZ=0 EndX=30.48 EndY=64.897 EndZ=0
    g10: LineSegment StartX=30.48 StartY=64.897 StartZ=0 EndX=30.48 EndY=66.04 EndZ=0
    g11: LineSegment StartX=30.48 StartY=66.04 StartZ=0 EndX=1.27 EndY=66.04 EndZ=0
    g12: LineSegment StartX=31.75 StartY=63.373 StartZ=0 EndX=31.75 EndY=62.23 EndZ=0
  constraints (38):
    c: Vertical(g0)
    c: Coincident(g0,g1)
    c: Horizontal(g1)
    c: Coincident(g1,g2)
    c: Vertical(g2)
    c: Coincident(g2,g3)
    c: Horizontal(g3)
    c: Coincident(g3,g4)
    c: Vertical(g4)
    c: Coincident(g4,g5)
    c: Horizontal(g5)
    c: Coincident(g5,g6)
    c: Vertical(g6)
    c: Coincident(g6,g7)
    c: Horizontal(g7)
    c: Coincident(g7,g8)
    c: Vertical(g8)
    c: Coincident(g8,g9)
    c: Horizontal(g9)
    c: Coincident(g9,g10)
    c: Vertical(g10)
    c: Coincident(g10,g11)
    c: Coincident(g11,g0)
    c: Horizontal(g11)
    c: Equal(g3,g1)
    c: Equal(g1,g9)
    c: Equal(g9,g7)
    c: Equal(g0,g4)
    c: Equal(g4,g6)
    c: Equal(g8,g2)
    c: PointOnObject(g4,g-4)
    c: PointOnObject(g0,g-3)
    c: PointOnObject(g2,g-2)
    c: Coincident(g12,g7)
    c: Coincident(g12,g-4)
    c: Vertical(g12)
    c: DistanceX(g1,g0) = 1.27
    c: DistanceY(g2,g2) = 1.524
FEATURE [PartDesign::Pocket] Pocket007  label="case mockup bottom with rear guide"
  BaseFeature = -> Pad009
  Direction = (0,0,-1)
  Length = 10.16
  Length2 = 5
  Profile = -> Sketch018
  ReferenceAxis = -> Sketch018 [N_Axis]
  Type = 0
FEATURE [Sketcher::SketchObject] Sketch019  label="case mockup bottom floor guide plan"
  ExternalGeometry = -> [Pocket007]
  FullyConstrained = true
  MapMode = 5
  Placement = pos=(0,0,-6.35) rot=(0,0,1;0rad)
  Support = -> [Pocket007]
  sketch-geometry (12):
    g0: LineSegment StartX=1.27 StartY=64.897 StartZ=0 EndX=30.48 EndY=64.897 EndZ=0
    g1: LineSegment StartX=30.48 StartY=64.897 StartZ=0 EndX=30.48 EndY=66.04 EndZ=0
    g2: LineSegment StartX=30.48 StartY=66.04 StartZ=0 EndX=1.27 EndY=66.04 EndZ=0
    g3: LineSegment StartX=1.27 StartY=66.04 StartZ=0 EndX=1.27 EndY=64.897 EndZ=0
    g4: LineSegment StartX=1.27 StartY=63.373 StartZ=0 EndX=6.35 EndY=63.373 EndZ=0
    g5: LineSegment StartX=6.35 StartY=63.373 StartZ=0 EndX=6.35 EndY=62.23 EndZ=0
    g6: LineSegment StartX=6.35 StartY=62.23 StartZ=0 EndX=1.27 EndY=62.23 EndZ=0
    g7: LineSegment StartX=1.27 StartY=62.23 StartZ=0 EndX=1.27 EndY=63.373 EndZ=0
    g8: LineSegment StartX=30.48 StartY=63.373 StartZ=0 EndX=25.4 EndY=63.373 EndZ=0
    g9: LineSegment StartX=25.4 StartY=63.373 StartZ=0 EndX=25.4 EndY=62.23 EndZ=0
    g10: LineSegment StartX=25.4 StartY=62.23 StartZ=0 EndX=30.48 EndY=62.23 EndZ=0
    g11: LineSegment StartX=30.48 StartY=62.23 StartZ=0 EndX=30.48 EndY=63.373 EndZ=0
  constraints (32):
    c: Coincident(g0,g1)
    c: Coincident(g1,g2)
    c: Coincident(g2,g3)
    c: Coincident(g3,g0)
    c: Horizontal(g0)
    c: Horizontal(g2)
    c: Vertical(g1)
    c: Vertical(g3)
    c: Coincident(g0,g-6)
    c: Coincident(g1,g-3)
    c: Coincident(g4,g5)
    c: Coincident(g5,g6)
    c: Coincident(g6,g7)
    c: Coincident(g7,g4)
    c: Horizontal(g4)
    c: Horizontal(g6)
    c: Vertical(g5)
    c: Vertical(g7)
    c: Coincident(g4,g-5)
    c: PointOnObject(g5,g-4)
    c: Coincident(g8,g9)
    c: Coincident(g9,g10)
    c: Coincident(g10,g11)
    c: Coincident(g11,g8)
    c: Horizontal(g8)
    c: Horizontal(g10)
    c: Vertical(g9)
    c: Vertical(g11)
    c: Coincident(g8,g-8)
    c: PointOnObject(g9,g-4)
    c: Equal(g8,g4)
    c: DistanceX(g6,g6) = 5.08
FEATURE [PartDesign::Pad] Pad010  label="case mockup bottom with floor guide"
  BaseFeature = -> Pocket007
  Direction = (0,0,1)
  Length = 1.27
  Length2 = 10
  Profile = -> Sketch019
  ReferenceAxis = -> Sketch019 [N_Axis]
  Type = 0
FEATURE [PartDesign::Body] Body004  label="case mockup bottom body"
  Group = -> [Sketch008,Pad006,Sketch009,Pocket001,Sketch010,Pad007,Sketch011,Pocket002,Sketch012,Pad008,Sketch013,Pocket003,Sketch014,Pocket004,Sketch015,Pocket005,Sketch016,Pocket006,Sketch017,Pad009,Sketch018,Pocket007,Sketch019,Pad010]
  Origin = -> Origin004
  Tip = -> Pad010
FEATURE [PartDesign::FeatureBase] Clone003  label="case mockup bottom clone for ears"
  BaseFeature = -> Body004
FEATURE [Sketcher::SketchObject] Sketch020  label="case mockup bottom ears panel plan"
  ExternalGeometry = -> [Clone003]
  FullyConstrained = true
  MapMode = 5
  Placement = pos=(0,0,-8.89) rot=(1,0,0;3.14159rad)
  Support = -> [Clone003]
  sketch-geometry (45):
    g0: LineSegment StartX=-8.255 StartY=-17.4625 StartZ=0 EndX=-5.08 EndY=-17.4625 EndZ=0
    g1: LineSegment StartX=-5.08 StartY=-17.4625 StartZ=0 EndX=-5.08 EndY=-46.0375 EndZ=0
    g2: LineSegment StartX=-5.08 StartY=-46.0375 StartZ=0 EndX=-8.255 EndY=-46.0375 EndZ=0
    g3: LineSegment StartX=-8.255 StartY=-46.0375 StartZ=0 EndX=-8.255 EndY=-17.4625 EndZ=0
    g4: LineSegment StartX=36.83 StartY=-17.4625 StartZ=0 EndX=40.005 EndY=-17.4625 EndZ=0
    g5: LineSegment StartX=40.005 StartY=-17.4625 StartZ=0 EndX=40.005 EndY=-46.0375 EndZ=0
    g6: LineSegment StartX=40.005 StartY=-46.0375 StartZ=0 EndX=36.83 EndY=-46.0375 EndZ=0
    g7: LineSegment StartX=36.83 StartY=-46.0375 StartZ=0 EndX=36.83 EndY=-17.4625 EndZ=0
    g8: LineSegment StartX=-9.525 StartY=-6.35 StartZ=0 EndX=41.275 EndY=-6.35 EndZ=0
    g9: LineSegment StartX=41.275 StartY=-6.35 StartZ=0 EndX=41.275 EndY=-57.15 EndZ=0
    g10: LineSegment StartX=41.275 StartY=-57.15 StartZ=0 EndX=-9.525 EndY=-57.15 EndZ=0
    g11: LineSegment StartX=-9.525 StartY=-57.15 StartZ=0 EndX=-9.525 EndY=-6.35 EndZ=0
    g12: Circle CenterX=-9.525 CenterY=-6.35 CenterZ=0 NormalX=0 NormalY=0 NormalZ=1 AngleXU=0 Radius=3.556
    g13: Circle CenterX=41.275 CenterY=-6.35 CenterZ=0 NormalX=0 NormalY=0 NormalZ=1 AngleXU=0 Radius=3.556
    g14: Circle CenterX=41.275 CenterY=-57.15 CenterZ=0 NormalX=0 NormalY=0 NormalZ=1 AngleXU=0 Radius=3.556
    g15: Circle CenterX=-9.525 CenterY=-57.15 CenterZ=0 NormalX=0 NormalY=0 NormalZ=1 AngleXU=0 Radius=3.556
    g16: LineSegment StartX=34.29 StartY=2.54 StartZ=0 EndX=41.275 EndY=2.54 EndZ=0
    g17: LineSegment StartX=41.275 StartY=2.54 StartZ=0 EndX=41.275 EndY=-6.35 EndZ=0
    g18: LineSegment StartX=41.275 StartY=-57.15 StartZ=0 EndX=41.275 EndY=-66.04 EndZ=0
    g19: LineSegment StartX=41.275 StartY=-66.04 StartZ=0 EndX=34.29 EndY=-66.04 EndZ=0
    g20: LineSegment StartX=-2.54 StartY=-66.04 StartZ=0 EndX=-9.525 EndY=-66.04 EndZ=0
    g21: LineSegment StartX=-9.525 StartY=-66.04 StartZ=0 EndX=-9.525 EndY=-57.15 EndZ=0
    g22: LineSegment StartX=-9.525 StartY=-6.35 StartZ=0 EndX=-9.525 EndY=2.54 EndZ=0
    g23: LineSegment StartX=-9.525 StartY=2.54 StartZ=0 EndX=-2.54 EndY=2.54 EndZ=0
    g24: LineSegment StartX=-2.54 StartY=2.54 StartZ=0 EndX=-2.54 EndY=-66.04 EndZ=0
    g25: LineSegment StartX=34.29 StartY=2.54 StartZ=0 EndX=34.29 EndY=-66.04 EndZ=0
    g26: LineSegment StartX=-9.525 StartY=-6.35 StartZ=0 EndX=-18.415 EndY=-6.35 EndZ=0
    g27: LineSegment StartX=-18.415 StartY=-6.35 StartZ=0 EndX=-18.415 EndY=-57.15 EndZ=0
    g28: LineSegment StartX=-18.415 StartY=-57.15 StartZ=0 EndX=-9.525 EndY=-57.15 EndZ=0
    g29: LineSegment StartX=41.275 StartY=-57.15 StartZ=0 EndX=50.165 EndY=-57.15 EndZ=0
    g30: LineSegment StartX=50.165 StartY=-57.15 StartZ=0 EndX=50.165 EndY=-6.35 EndZ=0
    g31: LineSegment StartX=50.165 StartY=-6.35 StartZ=0 EndX=41.275 EndY=-6.35 EndZ=0
    g32: ArcOfCircle CenterX=-9.525 CenterY=-6.35 CenterZ=0 NormalX=0 NormalY=0 NormalZ=1 AngleXU=0 Radius=8.89 StartAngle=1.5708 EndAngle=3.14159
    g33: ArcOfCircle CenterX=-9.525 CenterY=-57.15 CenterZ=0 NormalX=0 NormalY=0 NormalZ=1 AngleXU=0 Radius=8.89 StartAngle=3.14159 EndAngle=4.71239
    g34: ArcOfCircle CenterX=41.275 CenterY=-57.15 CenterZ=0 NormalX=0 NormalY=0 NormalZ=1 AngleXU=0 Radius=8.89 StartAngle=4.71239 EndAngle=6.28319
    g35: ArcOfCircle CenterX=41.275 CenterY=-6.35 CenterZ=0 NormalX=0 NormalY=0 NormalZ=1 AngleXU=0 Radius=8.89 StartAngle=0 EndAngle=1.5708
    g36: LineSegment StartX=-5.08 StartY=-17.4625 StartZ=0 EndX=36.83 EndY=-17.4625 EndZ=0
    g37: LineSegment StartX=-5.08 StartY=-46.0375 StartZ=0 EndX=36.83 EndY=-46.0375 EndZ=0
    g38: LineSegment StartX=-8.255 StartY=-17.4625 StartZ=0 EndX=-9.525 EndY=-17.4625 EndZ=0
    g39: LineSegment StartX=40.005 StartY=-17.4625 StartZ=0 EndX=41.275 EndY=-17.4625 EndZ=0
    g40: LineSegment StartX=-2.54 StartY=-66.04 StartZ=0 EndX=15.875 EndY=-31.75 EndZ=0
    g41: LineSegment StartX=15.875 StartY=-31.75 StartZ=0 EndX=34.29 EndY=2.54 EndZ=0
    g42: LineSegment StartX=40.005 StartY=-17.4625 StartZ=0 EndX=38.4175 EndY=-31.75 EndZ=0
    g43: LineSegment StartX=38.4175 StartY=-31.75 StartZ=0 EndX=36.83 EndY=-46.0375 EndZ=0
    g44: LineSegment StartX=15.875 StartY=-31.75 StartZ=0 EndX=38.4175 EndY=-31.75 EndZ=0
  constraints (114):
    c: Coincident(g0,g1)
    c: Coincident(g1,g2)
    c: Coincident(g2,g3)
    c: Coincident(g3,g0)
    c: Horizontal(g0)
    c: Horizontal(g2)
    c: Vertical(g1)
    c: Vertical(g3)
    c: Coincident(g4,g5)
    c: Coincident(g5,g6)
    c: Coincident(g6,g7)
    c: Coincident(g7,g4)
    c: Horizontal(g4)
    c: Horizontal(g6)
    c: Vertical(g5)
    c: Vertical(g7)
    c: Coincident(g8,g9)
    c: Coincident(g9,g10)
    c: Coincident(g10,g11)
    c: Coincident(g11,g8)
    c: Horizontal(g8)
    c: Horizontal(g10)
    c: Vertical(g9)
    c: Vertical(g11)
    c: Coincident(g12,g8)
    c: Coincident(g13,g8)
    c: Coincident(g14,g9)
    c: Coincident(g15,g10)
    c: Equal(g14,g13)
    c: Equal(g14,g12)
    c: Equal(g14,g15)
    c: Diameter(g14) = 7.112
    c: DistanceY(g9,g9) = 50.8
    c: DistanceX(g10,g10) = 50.8
    c: Horizontal(g16)
    c: Coincident(g16,g17)
    c: Coincident(g17,g13)
    c: Vertical(g17)
    c: Coincident(g18,g14)
    c: Vertical(g18)
    c: Coincident(g18,g19)
    c: Coincident(g19,g-4)
    c: Horizontal(g19)
    c: Horizontal(g20)
    c: Coincident(g20,g21)
    c: Coincident(g21,g15)
    c: Vertical(g21)
    c: Coincident(g22,g12)
    c: Vertical(g22)
    c: Coincident(g23,g22)
    c: Coincident(g23,g-3)
    c: Horizontal(g23)
    c: Coincident(g16,g-3)
    c: Coincident(g20,g-4)
    c: Equal(g23,g16)
    c: Coincident(g24,g23)
    c: Coincident(g25,g16)
    c: Coincident(g25,g19)
    c: Coincident(g24,g20)
    c: Coincident(g26,g12)
    c: Horizontal(g26)
    c: Coincident(g26,g27)
    c: Coincident(g27,g28)
    c: Coincident(g28,g15)
    c: Horizontal(g28)
    c: Coincident(g29,g14)
    c: Horizontal(g29)
    c: Coincident(g29,g30)
    c: Coincident(g30,g31)
    c: Coincident(g31,g13)
    c: Horizontal(g31)
    c: Equal(g21,g22)
    c: Coincident(g32,g12)
    c: Coincident(g32,g23)
    c: Coincident(g32,g27)
    c: Coincident(g33,g15)
    c: Coincident(g33,g27)
    c: Coincident(g33,g20)
    c: Coincident(g34,g14)
    c: Coincident(g34,g19)
    c: Coincident(g34,g30)
    c: Coincident(g35,g13)
    c: Coincident(g35,g16)
    c: Coincident(g35,g30)
    c: Coincident(g36,g0)
    c: Coincident(g36,g4)
    c: Horizontal(g36)
    c: Coincident(g37,g1)
    c: Coincident(g37,g6)
    c: Horizontal(g37)
    c: Equal(g0,g4)
    c: Coincident(g38,g0)
    c: PointOnObject(g38,g11)
    c: Horizontal(g38)
    c: Coincident(g39,g4)
    c: PointOnObject(g39,g9)
    c: Horizontal(g39)
    c: Equal(g39,g38)
    c: DistanceX(g2,g2) = 3.175
    c: DistanceX(g38,g38) = 1.27
    c: DistanceY(g3,g3) = 28.575
    c: Coincident(g20,g40)
    c: Coincident(g40,g41)
    c: Coincident(g41,g16)
    c: Coincident(g4,g42)
    c: Coincident(g42,g43)
    c: Coincident(g43,g6)
    c: Parallel(g43,g42)
    c: Equal(g42,g43)
    c: Parallel(g41,g40)
    c: Equal(g41,g40)
    c: Coincident(g44,g40)
    c: Coincident(g44,g42)
    c: Horizontal(g44)
FEATURE [PartDesign::Pad] Pad011  label="case mockup bottom ears with slab"
  BaseFeature = -> Clone003
  Direction = (0,0,-1)
  Length = 2.54
  Length2 = 10
  Profile = -> Sketch020
  ReferenceAxis = -> Sketch020 [N_Axis]
  Reversed = true
  Type = 0
FEATURE [Sketcher::SketchObject] Sketch021  label="case mockup bottom ears ridge plan"
  ExternalGeometry = -> [Pad011]
  FullyConstrained = true
  MapMode = 5
  Placement = pos=(0,0,-8.89) rot=(1,0,0;3.14159rad)
  Support = -> [Pad011]
  sketch-geometry (52):
    g0: Circle CenterX=-9.525 CenterY=-57.15 CenterZ=0 NormalX=0 NormalY=0 NormalZ=1 AngleXU=0 Radius=3.556
    g1: Circle CenterX=41.275 CenterY=-57.15 CenterZ=0 NormalX=0 NormalY=0 NormalZ=1 AngleXU=0 Radius=3.556
    g2: Circle CenterX=-9.525 CenterY=-6.35 CenterZ=0 NormalX=0 NormalY=0 NormalZ=1 AngleXU=0 Radius=3.556
    g3: Circle CenterX=41.275 CenterY=-6.35 CenterZ=0 NormalX=0 NormalY=0 NormalZ=1 AngleXU=0 Radius=3.556
    g4: LineSegment StartX=-10.795 StartY=-51.1878 StartZ=0 EndX=-10.795 EndY=-12.3122 EndZ=0
    g5: LineSegment StartX=42.545 StartY=-51.1878 StartZ=0 EndX=42.545 EndY=-12.3122 EndZ=0
    g6: LineSegment StartX=-3.56276 StartY=-5.08 StartZ=0 EndX=35.3128 EndY=-5.08 EndZ=0
    g7: LineSegment StartX=35.3128 StartY=-5.08 StartZ=0 EndX=35.3128 EndY=-7.62 EndZ=0
    g8: LineSegment StartX=35.3128 StartY=-7.62 StartZ=0 EndX=-3.56276 EndY=-7.62 EndZ=0
    g9: LineSegment StartX=-3.56276 StartY=-7.62 StartZ=0 EndX=-3.56276 EndY=-5.08 EndZ=0
    g10: LineSegment StartX=-3.56276 StartY=-55.88 StartZ=0 EndX=35.3128 EndY=-55.88 EndZ=0
    g11: LineSegment StartX=35.3128 StartY=-55.88 StartZ=0 EndX=35.3128 EndY=-58.42 EndZ=0
    g12: LineSegment StartX=35.3128 StartY=-58.42 StartZ=0 EndX=-3.56276 EndY=-58.42 EndZ=0
    g13: LineSegment StartX=-3.56276 StartY=-58.42 StartZ=0 EndX=-3.56276 EndY=-55.88 EndZ=0
    g14: ArcOfCircle CenterX=-9.525 CenterY=-57.15 CenterZ=0 NormalX=0 NormalY=0 NormalZ=1 AngleXU=0 Radius=6.096 StartAngle=0.209871 EndAngle=1.36093
    g15: ArcOfCircle CenterX=41.275 CenterY=-57.15 CenterZ=0 NormalX=0 NormalY=0 NormalZ=1 AngleXU=0 Radius=6.096 StartAngle=1.78067 EndAngle=2.93172
    g16: ArcOfCircle CenterX=41.275 CenterY=-6.35 CenterZ=0 NormalX=0 NormalY=0 NormalZ=1 AngleXU=0 Radius=6.096 StartAngle=3.35146 EndAngle=4.50252
    g17: ArcOfCircle CenterX=-9.525 CenterY=-6.35 CenterZ=0 NormalX=0 NormalY=0 NormalZ=1 AngleXU=0 Radius=6.096 StartAngle=4.92226 EndAngle=6.07331
    g18: LineSegment StartX=-9.525 StartY=-57.15 StartZ=0 EndX=-9.525 EndY=-6.35 EndZ=0
    g19: LineSegment StartX=-8.255 StartY=-17.4625 StartZ=0 EndX=-9.525 EndY=-17.4625 EndZ=0
    g20: LineSegment StartX=-9.525 StartY=-17.4625 StartZ=0 EndX=-10.795 EndY=-17.4625 EndZ=0
    g21: LineSegment StartX=-8.255 StartY=-17.4625 StartZ=0 EndX=-5.08 EndY=-17.4625 EndZ=0
    g22: LineSegment StartX=-5.08 StartY=-17.4625 StartZ=0 EndX=-5.08 EndY=-46.0375 EndZ=0
    g23: LineSegment StartX=-5.08 StartY=-46.0375 StartZ=0 EndX=-8.255 EndY=-46.0375 EndZ=0
    g24: LineSegment StartX=-8.255 StartY=-46.0375 StartZ=0 EndX=-8.255 EndY=-17.4625 EndZ=0
    g25: LineSegment StartX=40.005 StartY=-17.4625 StartZ=0 EndX=36.83 EndY=-17.4625 EndZ=0
    g26: LineSegment StartX=36.83 StartY=-17.4625 StartZ=0 EndX=36.83 EndY=-46.0375 EndZ=0
    g27: LineSegment StartX=36.83 StartY=-46.0375 StartZ=0 EndX=40.005 EndY=-46.0375 EndZ=0
    g28: LineSegment StartX=40.005 StartY=-46.0375 StartZ=0 EndX=40.005 EndY=-17.4625 EndZ=0
    g29: LineSegment StartX=-8.255 StartY=-12.3122 StartZ=0 EndX=-8.255 EndY=-14.9225 EndZ=0
    g30: LineSegment StartX=-8.255 StartY=-14.9225 StartZ=0 EndX=-2.54 EndY=-14.9225 EndZ=0
    g31: LineSegment StartX=-2.54 StartY=-14.9225 StartZ=0 EndX=-2.54 EndY=-48.5775 EndZ=0
    g32: LineSegment StartX=-2.54 StartY=-48.5775 StartZ=0 EndX=-8.255 EndY=-48.5775 EndZ=0
    g33: LineSegment StartX=-8.255 StartY=-48.5775 StartZ=0 EndX=-8.255 EndY=-51.1878 EndZ=0
    g34: ArcOfCircle CenterX=-9.525 CenterY=-6.35 CenterZ=0 NormalX=0 NormalY=0 NormalZ=1 AngleXU=0 Radius=6.096 StartAngle=0.209871 EndAngle=4.50252
    g35: ArcOfCircle CenterX=-9.525 CenterY=-57.15 CenterZ=0 NormalX=0 NormalY=0 NormalZ=1 AngleXU=0 Radius=6.096 StartAngle=1.78067 EndAngle=6.07331
    g36: LineSegment StartX=-8.255 StartY=-46.0375 StartZ=0 EndX=-10.795 EndY=-46.0375 EndZ=0
    g37: LineSegment StartX=-5.08 StartY=-46.0375 StartZ=0 EndX=-2.54 EndY=-46.0375 EndZ=0
    g38: LineSegment StartX=-8.255 StartY=-48.5775 StartZ=0 EndX=-8.255 EndY=-46.0375 EndZ=0
    g39: LineSegment StartX=-8.255 StartY=-14.9225 StartZ=0 EndX=-8.255 EndY=-46.0375 EndZ=0
    g40: LineSegment StartX=40.005 StartY=-12.3122 StartZ=0 EndX=40.005 EndY=-14.9225 EndZ=0
    g41: LineSegment StartX=40.005 StartY=-14.9225 StartZ=0 EndX=34.29 EndY=-14.9225 EndZ=0
    g42: LineSegment StartX=34.29 StartY=-14.9225 StartZ=0 EndX=34.29 EndY=-48.5775 EndZ=0
    g43: LineSegment StartX=34.29 StartY=-48.5775 StartZ=0 EndX=40.005 EndY=-48.5775 EndZ=0
    g44: LineSegment StartX=40.005 StartY=-48.5775 StartZ=0 EndX=40.005 EndY=-51.1878 EndZ=0
    g45: ArcOfCircle CenterX=41.275 CenterY=-57.15 CenterZ=0 NormalX=0 NormalY=0 NormalZ=1 AngleXU=0 Radius=6.096 StartAngle=3.35146 EndAngle=7.64411
    g46: ArcOfCircle CenterX=41.275 CenterY=-6.35 CenterZ=0 NormalX=0 NormalY=0 NormalZ=1 AngleXU=0 Radius=6.096 StartAngle=4.92226 EndAngle=9.21491
    g47: LineSegment StartX=36.83 StartY=-17.4625 StartZ=0 EndX=34.29 EndY=-17.4625 EndZ=0
    g48: LineSegment StartX=40.005 StartY=-17.4625 StartZ=0 EndX=42.545 EndY=-17.4625 EndZ=0
    g49: LineSegment StartX=-2.54 StartY=-14.9225 StartZ=0 EndX=34.29 EndY=-14.9225 EndZ=0
    g50: LineSegment StartX=40.005 StartY=-14.9225 StartZ=0 EndX=40.005 EndY=-48.5775 EndZ=0
    g51: LineSegment StartX=-2.54 StartY=-48.5775 StartZ=0 EndX=34.29 EndY=-48.5775 EndZ=0
  constraints (139):
    c: Coincident(g0,g-3)
    c: Coincident(g1,g-4)
    c: Coincident(g2,g-6)
    c: Coincident(g3,g-5)
    c: Equal(g-3,g0)
    c: Equal(g0,g1)
    c: Equal(g1,g3)
    c: Equal(g3,g2)
    c: Vertical(g4)
    c: Vertical(g5)
    c: Coincident(g6,g7)
    c: Coincident(g7,g8)
    c: Coincident(g8,g9)
    c: Coincident(g9,g6)
    c: Horizontal(g6)
    c: Horizontal(g8)
    c: Vertical(g7)
    c: Vertical(g9)
    c: Coincident(g10,g11)
    c: Coincident(g11,g12)
    c: Coincident(g12,g13)
    c: Coincident(g13,g10)
    c: Horizontal(g10)
    c: Horizontal(g12)
    c: Vertical(g11)
    c: Vertical(g13)
    c: Coincident(g14,g0)
    c: Coincident(g14,g10)
    c: Coincident(g15,g1)
    c: Coincident(g15,g10)
    c: Coincident(g16,g3)
    c: Coincident(g16,g8)
    c: Coincident(g17,g2)
    c: Coincident(g17,g8)
    c: Coincident(g18,g0)
    c: Coincident(g18,g2)
    c: Coincident(g19,g-7)
    c: PointOnObject(g19,g18)
    c: Horizontal(g19)
    c: Coincident(g19,g20)
    c: PointOnObject(g20,g4)
    c: Horizontal(g20)
    c: Equal(g19,g20)
    c: Coincident(g21,g22)
    c: Coincident(g22,g23)
    c: Coincident(g23,g24)
    c: Coincident(g24,g21)
    c: Horizontal(g21)
    c: Horizontal(g23)
    c: Vertical(g22)
    c: Vertical(g24)
    c: Coincident(g21,g19)
    c: Coincident(g22,g-8)
    c: Coincident(g25,g26)
    c: Coincident(g26,g27)
    c: Coincident(g27,g28)
    c: Coincident(g28,g25)
    c: Horizontal(g25)
    c: Horizontal(g27)
    c: Vertical(g26)
    c: Vertical(g28)
    c: Coincident(g25,g-9)
    c: Coincident(g26,g-10)
    c: Vertical(g29)
    c: Coincident(g29,g30)
    c: Horizontal(g30)
    c: Coincident(g30,g31)
    c: Vertical(g31)
    c: Coincident(g31,g32)
    c: Horizontal(g32)
    c: Coincident(g32,g33)
    c: Vertical(g33)
    c: Coincident(g34,g2)
    c: Coincident(g34,g6)
    c: Coincident(g35,g0)
    c: Coincident(g35,g12)
    c: Equal(g35,g14)
    c: Equal(g34,g17)
    c: DistanceY(g11,g11) = 2.54
    c: Diameter(g15) = 12.192
    c: Equal(g14,g15)
    c: Equal(g17,g14)
    c: Equal(g16,g15)
    c: Equal(g7,g11)
    c: Coincident(g36,g23)
    c: PointOnObject(g36,g4)
    c: Horizontal(g36)
    c: Coincident(g37,g22)
    c: PointOnObject(g37,g31)
    c: Horizontal(g37)
    c: Equal(g37,g36)
    c: Coincident(g38,g32)
    c: PointOnObject(g38,g37)
    c: Vertical(g38)
    c: Equal(g38,g37)
    c: Coincident(g39,g29)
    c: Coincident(g39,g38)
    c: Vertical(g39)
    c: Vertical(g40)
    c: Coincident(g40,g41)
    c: Horizontal(g41)
    c: Coincident(g41,g42)
    c: Vertical(g42)
    c: Coincident(g42,g43)
    c: Horizontal(g43)
    c: Coincident(g43,g44)
    c: Vertical(g44)
    c: Coincident(g45,g1)
    c: Coincident(g45,g12)
    c: Coincident(g46,g3)
    c: Coincident(g46,g6)
    c: Coincident(g47,g25)
    c: PointOnObject(g47,g42)
    c: Horizontal(g47)
    c: Coincident(g48,g25)
    c: PointOnObject(g48,g5)
    c: Horizontal(g48)
    c: Equal(g48,g47)
    c: Equal(g47,g36)
    c: Coincident(g49,g30)
    c: Coincident(g49,g41)
    c: Horizontal(g49)
    c: Coincident(g50,g40)
    c: Coincident(g50,g43)
    c: Vertical(g50)
    c: Equal(g40,g29)
    c: Coincident(g51,g31)
    c: Coincident(g51,g42)
    c: Horizontal(g51)
    c: Equal(g29,g33)
    c: Coincident(g4,g34)
    c: Coincident(g5,g46)
    c: Coincident(g4,g35)
    c: Coincident(g5,g45)
    c: Coincident(g29,g17)
    c: Coincident(g33,g14)
    c: PointOnObject(g21,g39)
    c: Coincident(g44,g15)
    c: Coincident(g40,g16)
FEATURE [PartDesign::Pad] Pad012  label="case mockup bottom ears with ridges"
  BaseFeature = -> Pad011
  Direction = (0,0,-1)
  Length = 3.175
  Length2 = 10
  Profile = -> Sketch021
  ReferenceAxis = -> Sketch021 [N_Axis]
  Type = 0
FEATURE [Sketcher::SketchObject] Sketch022  label="screw 4-40 profile"
  FullyConstrained = true
  MapMode = 5
  Placement = pos=(0,0,0) rot=(1,0,0;1.5708rad)
  Support = -> [XZ_Plane008]
  sketch-geometry (6):
    g0: LineSegment StartX=0 StartY=2.1082 StartZ=0 EndX=0 EndY=-9.525 EndZ=0
    g1: LineSegment StartX=0 StartY=-9.525 StartZ=0 EndX=1.4224 EndY=-9.525 EndZ=0
    g2: LineSegment StartX=1.4224 StartY=-9.525 StartZ=0 EndX=1.4224 EndY=0 EndZ=0
    g3: LineSegment StartX=1.4224 StartY=0 StartZ=0 EndX=2.794 EndY=0 EndZ=0
    g4: LineSegment StartX=2.794 StartY=0 StartZ=0 EndX=2.794 EndY=2.1082 EndZ=0
    g5: LineSegment StartX=2.794 StartY=2.1082 StartZ=0 EndX=0 EndY=2.1082 EndZ=0
  constraints (18):
    c: Vertical(g0)
    c: Coincident(g0,g1)
    c: Horizontal(g1)
    c: Coincident(g1,g2)
    c: Vertical(g2)
    c: Coincident(g2,g3)
    c: Horizontal(g3)
    c: Coincident(g3,g4)
    c: Vertical(g4)
    c: Coincident(g4,g5)
    c: Coincident(g5,g0)
    c: Horizontal(g5)
    c: PointOnObject(g0,g-2)
    c: PointOnObject(g2,g-1)
    c: DistanceX(g1,g1) = 1.4224
    c: DistanceY(g1,g3) = 9.525
    c: DistanceX(g5,g5) = 2.794
    c: DistanceY(g4,g4) = 2.1082
FEATURE [PartDesign::Revolution] Revolution001  label="screw 4-40 revolved"
  Angle = 360
  Axis = (0,2e-16,1)
  Base = (0,0,0)
  Placement = pos=(0,0,0) rot=(1,0,0;1.5708rad)
  Profile = -> Sketch022
  ReferenceAxis = -> Sketch022 [V_Axis]
  Reversed = true
FEATURE [PartDesign::Body] Body008  label="screw 4-40 body"
  Group = -> [Sketch022,Revolution001]
  Origin = -> Origin008
  Tip = -> Revolution001
FEATURE [PartDesign::FeatureBase] Clone005
  BaseFeature = -> Body008
FEATURE [PartDesign::Body] Body009  label="case screw copy 1"
  BaseFeature = -> Body008
  Group = -> [Clone005]
  Origin = -> Origin009
  Placement = pos=(7.62,22.225,-4.1275) rot=(1,0,0;3.14159rad)
  Tip = -> Clone005
FEATURE [PartDesign::FeatureBase] Clone006
  BaseFeature = -> Body008
FEATURE [PartDesign::Body] Body010  label="case screw copy 2"
  BaseFeature = -> Body008
  Group = -> [Clone006]
  Origin = -> Origin010
  Placement = pos=(7.62,50.8,1.27) rot=(1,0,0;3.14159rad)
  Tip = -> Clone006
FEATURE [PartDesign::FeatureBase] Clone007
  BaseFeature = -> Body008
FEATURE [PartDesign::Body] Body011  label="case screw copy 3"
  BaseFeature = -> Body008
  Group = -> [Clone007]
  Origin = -> Origin011
  Placement = pos=(24.13,50.8,1.27) rot=(1,0,0;3.14159rad)
  Tip = -> Clone007
FEATURE [Sketcher::SketchObject] Sketch023  label="screw 1f4-20 profile"
  FullyConstrained = true
  MapMode = 5
  Placement = pos=(0,0,0) rot=(1,0,0;1.5708rad)
  Support = -> [XZ_Plane012]
  sketch-geometry (6):
    g0: LineSegment StartX=0 StartY=4.445 StartZ=0 EndX=6.2484 EndY=4.445 EndZ=0
    g1: LineSegment StartX=6.2484 StartY=4.445 StartZ=0 EndX=6.2484 EndY=0 EndZ=0
    g2: LineSegment StartX=6.2484 StartY=0 StartZ=0 EndX=3.175 EndY=0 EndZ=0
    g3: LineSegment StartX=3.175 StartY=0 StartZ=0 EndX=3.175 EndY=-9.525 EndZ=0
    g4: LineSegment StartX=3.175 StartY=-9.525 StartZ=0 EndX=0 EndY=-9.525 EndZ=0
    g5: LineSegment StartX=0 StartY=-9.525 StartZ=0 EndX=0 EndY=4.445 EndZ=0
  constraints (18):
    c: Horizontal(g0)
    c: Coincident(g0,g1)
    c: Vertical(g1)
    c: Coincident(g1,g2)
    c: Horizontal(g2)
    c: Coincident(g2,g3)
    c: Vertical(g3)
    c: Coincident(g3,g4)
    c: Horizontal(g4)
    c: Coincident(g4,g5)
    c: Coincident(g5,g0)
    c: Vertical(g5)
    c: PointOnObject(g0,g-2)
    c: PointOnObject(g2,g-1)
    c: DistanceX(g4,g4) = 3.175
    c: DistanceY(g4,g-1) = 9.525
    c: DistanceX(g0,g0) = 6.2484
    c: DistanceY(g1,g1) = 4.445
FEATURE [PartDesign::Revolution] Revolution002  label="screw 1f4-20 revolved"
  Angle = 360
  Axis = (0,2e-16,1)
  Base = (0,0,0)
  Placement = pos=(0,0,0) rot=(1,0,0;1.5708rad)
  Profile = -> Sketch023
  ReferenceAxis = -> Sketch023 [V_Axis]
  Reversed = true
FEATURE [PartDesign::Body] Body012  label="screw 1f4-20 body"
  Group = -> [Sketch023,Revolution002]
  Origin = -> Origin012
  Tip = -> Revolution002
FEATURE [App::DocumentObjectGroup] Group005  label="screw parts"
  Group = -> [Body008,Body012]
FEATURE [PartDesign::FeatureBase] Clone008
  BaseFeature = -> Body012
FEATURE [PartDesign::Body] Body013  label="mounting screw copy 1"
  BaseFeature = -> Body012
  Group = -> [Clone008]
  Origin = -> Origin013
  Placement = pos=(-9.525,6.35,-6.35) rot=(0,0,1;0rad)
  Tip = -> Clone008
FEATURE [PartDesign::FeatureBase] Clone009
  BaseFeature = -> Body012
FEATURE [PartDesign::Body] Body014  label="mounting screw copy 2"
  BaseFeature = -> Body012
  Group = -> [Clone009]
  Origin = -> Origin014
  Placement = pos=(41.275,6.35,-6.35) rot=(0,0,1;0rad)
  Tip = -> Clone009
FEATURE [PartDesign::FeatureBase] Clone010
  BaseFeature = -> Body012
FEATURE [PartDesign::Body] Body015  label="mounting screw copy 3"
  BaseFeature = -> Body012
  Group = -> [Clone010]
  Origin = -> Origin015
  Placement = pos=(-9.525,57.15,-6.35) rot=(0,0,1;0rad)
  Tip = -> Clone010
FEATURE [PartDesign::FeatureBase] Clone011
  BaseFeature = -> Body012
FEATURE [PartDesign::Body] Body016  label="mounting screw copy 4"
  BaseFeature = -> Body012
  Group = -> [Clone011]
  Origin = -> Origin016
  Placement = pos=(41.275,57.15,-6.35) rot=(0,0,1;0rad)
  Tip = -> Clone011
FEATURE [Sketcher::SketchObject] Sketch024  label="case mockup plate plan"
  FullyConstrained = true
  MapMode = 5
  Placement = pos=(0,0,0) rot=(1,0,0;1.5708rad)
  Support = -> [XZ_Plane017]
  sketch-geometry (9):
    g0: LineSegment StartX=-15.6845 StartY=15.6845 StartZ=0 EndX=15.6845 EndY=15.6845 EndZ=0
    g1: LineSegment StartX=15.6845 StartY=15.6845 StartZ=0 EndX=15.6845 EndY=-6.1595 EndZ=0
    g2: LineSegment StartX=15.6845 StartY=-6.1595 StartZ=0 EndX=-15.6845 EndY=-6.1595 EndZ=0
    g3: LineSegment StartX=-15.6845 StartY=-6.1595 StartZ=0 EndX=-15.6845 EndY=15.6845 EndZ=0
    g4: LineSegment StartX=-15.6845 StartY=-6.1595 StartZ=0 EndX=0 EndY=0 EndZ=0
    g5: LineSegment StartX=0 StartY=0 StartZ=0 EndX=15.6845 EndY=-6.1595 EndZ=0
    g6: Circle CenterX=0 CenterY=4.7625 CenterZ=0 NormalX=0 NormalY=0 NormalZ=1 AngleXU=0 Radius=8.001
    g7: LineSegment StartX=-15.6845 StartY=15.6845 StartZ=0 EndX=0 EndY=4.7625 EndZ=0
    g8: LineSegment StartX=0 StartY=4.7625 StartZ=0 EndX=-15.6845 EndY=-6.1595 EndZ=0
  constraints (23):
    c: Coincident(g0,g1)
    c: Coincident(g1,g2)
    c: Coincident(g2,g3)
    c: Coincident(g3,g0)
    c: Horizontal(g0)
    c: Horizontal(g2)
    c: Vertical(g1)
    c: Vertical(g3)
    c: Coincident(g2,g4)
    c: Coincident(g4,g-1)
    c: Coincident(g4,g5)
    c: Coincident(g5,g1)
    c: Equal(g5,g4)
    c: DistanceX(g2,g2) = 31.369
    c: DistanceY(g2,g4) = 6.1595
    c: DistanceY(g1,g1) = 21.844
    c: PointOnObject(g6,g-2)
    c: Coincident(g0,g7)
    c: Coincident(g7,g6)
    c: Coincident(g7,g8)
    c: Coincident(g2,g8)
    c: Equal(g8,g7)
    c: Diameter(g6) = 16.002
FEATURE [PartDesign::Pad] Pad013  label="case mockup plate slab"
  Direction = (0,-1,2e-16)
  Length = 2.54
  Length2 = 10
  Placement = pos=(0,0,0) rot=(1,0,0;1.5708rad)
  Profile = -> Sketch024
  ReferenceAxis = -> Sketch024 [N_Axis]
  Type = 0
FEATURE [Sketcher::SketchObject] Sketch025  label="case mockup plate flange plan"
  ExternalGeometry = -> [Pad013]
  FullyConstrained = true
  MapMode = 5
  Placement = pos=(0,0,0) rot=(-1,0,0;1.5708rad)
  Support = -> [Pad013]
  sketch-geometry (16):
    g0: LineSegment StartX=-14.4145 StartY=4.8895 StartZ=0 EndX=14.4145 EndY=4.8895 EndZ=0
    g1: LineSegment StartX=14.4145 StartY=4.8895 StartZ=0 EndX=14.4145 EndY=-14.4145 EndZ=0
    g2: LineSegment StartX=14.4145 StartY=-14.4145 StartZ=0 EndX=-14.4145 EndY=-14.4145 EndZ=0
    g3: LineSegment StartX=-14.4145 StartY=-14.4145 StartZ=0 EndX=-14.4145 EndY=4.8895 EndZ=0
    g4: LineSegment StartX=-22.0345 StartY=12.5095 StartZ=0 EndX=22.0345 EndY=12.5095 EndZ=0
    g5: LineSegment StartX=22.0345 StartY=12.5095 StartZ=0 EndX=22.0345 EndY=-22.0345 EndZ=0
    g6: LineSegment StartX=22.0345 StartY=-22.0345 StartZ=0 EndX=-22.0345 EndY=-22.0345 EndZ=0
    g7: LineSegment StartX=-22.0345 StartY=-22.0345 StartZ=0 EndX=-22.0345 EndY=12.5095 EndZ=0
    g8: LineSegment StartX=-22.0345 StartY=6.1595 StartZ=0 EndX=-15.6845 EndY=6.1595 EndZ=0
    g9: LineSegment StartX=-15.6845 StartY=6.1595 StartZ=0 EndX=-14.4145 EndY=6.1595 EndZ=0
    g10: LineSegment StartX=-14.4145 StartY=6.1595 StartZ=0 EndX=-14.4145 EndY=4.8895 EndZ=0
    g11: LineSegment StartX=-22.0345 StartY=12.5095 StartZ=0 EndX=-22.0345 EndY=6.1595 EndZ=0
    g12: LineSegment StartX=14.4145 StartY=-14.4145 StartZ=0 EndX=14.4145 EndY=-15.6845 EndZ=0
    g13: LineSegment StartX=14.4145 StartY=-15.6845 StartZ=0 EndX=15.6845 EndY=-15.6845 EndZ=0
    g14: LineSegment StartX=15.6845 StartY=-15.6845 StartZ=0 EndX=22.0345 EndY=-15.6845 EndZ=0
    g15: LineSegment StartX=22.0345 StartY=-15.6845 StartZ=0 EndX=22.0345 EndY=-22.0345 EndZ=0
  constraints (44):
    c: Coincident(g0,g1)
    c: Coincident(g1,g2)
    c: Coincident(g2,g3)
    c: Coincident(g3,g0)
    c: Horizontal(g0)
    c: Horizontal(g2)
    c: Vertical(g1)
    c: Vertical(g3)
    c: Coincident(g4,g5)
    c: Coincident(g5,g6)
    c: Coincident(g6,g7)
    c: Coincident(g7,g4)
    c: Horizontal(g4)
    c: Horizontal(g6)
    c: Vertical(g5)
    c: Vertical(g7)
    c: Coincident(g8,g-3)
    c: Coincident(g8,g9)
    c: Horizontal(g9)
    c: Coincident(g9,g10)
    c: Coincident(g10,g0)
    c: Coincident(g4,g11)
    c: Coincident(g1,g12)
    c: Coincident(g12,g13)
    c: Coincident(g13,g-4)
    c: Coincident(g13,g14)
    c: Horizontal(g14)
    c: Coincident(g14,g15)
    c: Coincident(g8,g11)
    c: Vertical(g10)
    c: Vertical(g12)
    c: Horizontal(g8)
    c: Horizontal(g13)
    c: Coincident(g5,g15)
    c: Equal(g8,g14)
    c: Equal(g9,g13)
    c: Equal(g10,g12)
    c: Equal(g11,g15)
    c: Vertical(g15)
    c: Equal(g10,g9)
    c: Equal(g11,g8)
    c: Vertical(g11)
    c: DistanceX(g8,g8) = 6.35
    c: DistanceX(g13,g13) = 1.27
FEATURE [PartDesign::Pocket] Pocket008  label="case mockup plate with flange"
  BaseFeature = -> Pad013
  Direction = (0,-1,2e-16)
  Length = 1.397
  Length2 = 5
  Placement = pos=(0,0,0) rot=(1,0,0;1.5708rad)
  Profile = -> Sketch025
  ReferenceAxis = -> Sketch025 [N_Axis]
  Type = 0
FEATURE [PartDesign::Body] Body017  label="case mockup plate body"
  Group = -> [Sketch024,Pad013,Sketch025,Pocket008]
  Origin = -> Origin017
  Tip = -> Pocket008
FEATURE [PartDesign::FeatureBase] Clone012
  BaseFeature = -> Body017
FEATURE [PartDesign::Body] Body018  label="case mockup plate clone"
  BaseFeature = -> Body017
  Group = -> [Clone012]
  Origin = -> Origin018
  Placement = pos=(15.875,66.04,0) rot=(0,0,1;0rad)
  Tip = -> Clone012
FEATURE [Sketcher::SketchObject] Sketch026  label="case mockup top footprint"
  FullyConstrained = true
  MapMode = 5
  Support = -> [XY_Plane019]
  sketch-geometry (12):
    g0: LineSegment StartX=-2.54 StartY=-2.54 StartZ=0 EndX=34.29 EndY=-2.54 EndZ=0
    g1: LineSegment StartX=34.29 StartY=-2.54 StartZ=0 EndX=34.29 EndY=66.04 EndZ=0
    g2: LineSegment StartX=34.29 StartY=66.04 StartZ=0 EndX=-2.54 EndY=66.04 EndZ=0
    g3: LineSegment StartX=-2.54 StartY=66.04 StartZ=0 EndX=-2.54 EndY=-2.54 EndZ=0
    g4: LineSegment StartX=0 StartY=0 StartZ=0 EndX=31.75 EndY=0 EndZ=0
    g5: LineSegment StartX=31.75 StartY=0 StartZ=0 EndX=31.75 EndY=63.5 EndZ=0
    g6: LineSegment StartX=31.75 StartY=63.5 StartZ=0 EndX=0 EndY=63.5 EndZ=0
    g7: LineSegment StartX=0 StartY=63.5 StartZ=0 EndX=0 EndY=0 EndZ=0
    g8: LineSegment StartX=31.75 StartY=66.04 StartZ=0 EndX=31.75 EndY=63.5 EndZ=0
    g9: LineSegment StartX=31.75 StartY=63.5 StartZ=0 EndX=34.29 EndY=63.5 EndZ=0
    g10: LineSegment StartX=-2.54 StartY=0 StartZ=0 EndX=0 EndY=0 EndZ=0
    g11: LineSegment StartX=0 StartY=0 StartZ=0 EndX=0 EndY=-2.54 EndZ=0
  constraints (35):
    c: Coincident(g0,g1)
    c: Coincident(g1,g2)
    c: Coincident(g2,g3)
    c: Coincident(g3,g0)
    c: Horizontal(g0)
    c: Horizontal(g2)
    c: Vertical(g1)
    c: Vertical(g3)
    c: Coincident(g4,g5)
    c: Coincident(g5,g6)
    c: Coincident(g6,g7)
    c: Coincident(g7,g4)
    c: Horizontal(g4)
    c: Horizontal(g6)
    c: Vertical(g5)
    c: Vertical(g7)
    c: Coincident(g4,g-1)
    c: PointOnObject(g8,g2)
    c: Coincident(g8,g5)
    c: Vertical(g8)
    c: Coincident(g8,g9)
    c: PointOnObject(g9,g1)
    c: Horizontal(g9)
    c: PointOnObject(g10,g3)
    c: Coincident(g10,g4)
    c: Coincident(g10,g11)
    c: PointOnObject(g11,g0)
    c: Vertical(g11)
    c: Horizontal(g10)
    c: Equal(g10,g11)
    c: Equal(g11,g8)
    c: Equal(g8,g9)
    c: DistanceY(g0,g10) = 2.54
    c: DistanceX(g4,g4) = 31.75
    c: DistanceY(g5,g5) = 63.5
FEATURE [PartDesign::Pad] Pad014  label="case mockup top slab"
  Direction = (0,0,1)
  Length = 2.54
  Length2 = 10
  Profile = -> Sketch026
  ReferenceAxis = -> Sketch026 [N_Axis]
  Type = 0
FEATURE [Sketcher::SketchObject] Sketch027  label="case mockup top wall plan"
  ExternalGeometry = -> [Pad014]
  FullyConstrained = true
  MapMode = 5
  Placement = pos=(0,0,0) rot=(1,0,0;3.14159rad)
  Support = -> [Pad014]
  sketch-geometry (12):
    g0: LineSegment StartX=-2.54 StartY=2.54 StartZ=0 EndX=34.29 EndY=2.54 EndZ=0
    g1: LineSegment StartX=34.29 StartY=2.54 StartZ=0 EndX=34.29 EndY=-66.04 EndZ=0
    g2: LineSegment StartX=34.29 StartY=-66.04 StartZ=0 EndX=-2.54 EndY=-66.04 EndZ=0
    g3: LineSegment StartX=-2.54 StartY=-66.04 StartZ=0 EndX=-2.54 EndY=2.54 EndZ=0
    g4: LineSegment StartX=0 StartY=0 StartZ=0 EndX=31.75 EndY=0 EndZ=0
    g5: LineSegment StartX=31.75 StartY=0 StartZ=0 EndX=31.75 EndY=-62.23 EndZ=0
    g6: LineSegment StartX=31.75 StartY=-62.23 StartZ=0 EndX=0 EndY=-62.23 EndZ=0
    g7: LineSegment StartX=0 StartY=-62.23 StartZ=0 EndX=0 EndY=0 EndZ=0
    g8: LineSegment StartX=-2.54 StartY=2.54 StartZ=0 EndX=-2.54 EndY=0 EndZ=0
    g9: LineSegment StartX=-2.54 StartY=0 StartZ=0 EndX=0 EndY=0 EndZ=0
    g10: LineSegment StartX=31.75 StartY=-62.23 StartZ=0 EndX=34.29 EndY=-62.23 EndZ=0
    g11: LineSegment StartX=31.75 StartY=-62.23 StartZ=0 EndX=31.75 EndY=-66.04 EndZ=0
  constraints (32):
    c: Coincident(g0,g1)
    c: Coincident(g1,g2)
    c: Coincident(g2,g3)
    c: Coincident(g3,g0)
    c: Horizontal(g0)
    c: Horizontal(g2)
    c: Vertical(g1)
    c: Vertical(g3)
    c: Coincident(g0,g-3)
    c: Coincident(g1,g-4)
    c: Coincident(g4,g5)
    c: Coincident(g5,g6)
    c: Coincident(g6,g7)
    c: Coincident(g7,g4)
    c: Horizontal(g4)
    c: Horizontal(g6)
    c: Vertical(g5)
    c: Vertical(g7)
    c: Coincident(g4,g-1)
    c: Coincident(g0,g8)
    c: Coincident(g8,g9)
    c: Coincident(g9,g4)
    c: Coincident(g5,g10)
    c: Coincident(g11,g5)
    c: Vertical(g11)
    c: Horizontal(g10)
    c: Equal(g9,g10)
    c: Horizontal(g9)
    c: Vertical(g8)
    c: PointOnObject(g11,g2)
    c: PointOnObject(g10,g1)
    c: DistanceY(g1,g10) = 3.81
FEATURE [PartDesign::Pad] Pad015  label="case mockup top with walls"
  BaseFeature = -> Pad014
  Direction = (0,0,-1)
  Length = 12.065
  Length2 = 10
  Profile = -> Sketch027
  ReferenceAxis = -> Sketch027 [N_Axis]
  Type = 0
FEATURE [Sketcher::SketchObject] Sketch028  label="case mockup top short post plan"
  ExternalGeometry = -> [Pad015]
  FullyConstrained = true
  MapMode = 5
  Placement = pos=(0,0,0) rot=(1,0,0;3.14159rad)
  Support = -> [Pad015]
  sketch-geometry (5):
    g0: LineSegment StartX=0 StartY=-62.23 StartZ=0 EndX=7.62 EndY=-50.8 EndZ=0
    g1: LineSegment StartX=7.62 StartY=-50.8 StartZ=0 EndX=24.13 EndY=-50.8 EndZ=0
    g2: LineSegment StartX=24.13 StartY=-50.8 StartZ=0 EndX=31.75 EndY=-62.23 EndZ=0
    g3: Circle CenterX=7.62 CenterY=-50.8 CenterZ=0 NormalX=0 NormalY=0 NormalZ=1 AngleXU=0 Radius=3.175
    g4: Circle CenterX=24.13 CenterY=-50.8 CenterZ=0 NormalX=0 NormalY=0 NormalZ=1 AngleXU=0 Radius=3.175
  constraints (12):
    c: Coincident(g-3,g0)
    c: Coincident(g0,g1)
    c: Horizontal(g1)
    c: Coincident(g1,g2)
    c: Coincident(g2,g-3)
    c: Equal(g0,g2)
    c: DistanceY(g0,g-1) = 50.8
    c: Coincident(g3,g0)
    c: Coincident(g4,g1)
    c: Equal(g3,g4)
    c: DistanceX(g2,g2) = 7.62
    c: Diameter(g3) = 6.35
FEATURE [PartDesign::Pad] Pad016  label="case mockup top with short posts"
  BaseFeature = -> Pad015
  Direction = (0,0,-1)
  Length = 12.065
  Length2 = 10
  Profile = -> Sketch028
  ReferenceAxis = -> Sketch028 [N_Axis]
  Type = 0
FEATURE [Sketcher::SketchObject] Sketch029  label="case mockup top short post hole plan"
  ExternalGeometry = -> [Pad016]
  FullyConstrained = true
  MapMode = 5
  Placement = pos=(0,0,-12.065) rot=(1,0,0;3.14159rad)
  Support = -> [Pad016]
  sketch-geometry (2):
    g0: Circle CenterX=7.62 CenterY=-50.8 CenterZ=0 NormalX=0 NormalY=0 NormalZ=1 AngleXU=0 Radius=1.143
    g1: Circle CenterX=24.13 CenterY=-50.8 CenterZ=0 NormalX=0 NormalY=0 NormalZ=1 AngleXU=0 Radius=1.143
  constraints (4):
    c: Coincident(g0,g-3)
    c: Coincident(g1,g-4)
    c: Equal(g1,g0)
    c: Diameter(g1) = 2.286
FEATURE [PartDesign::Pocket] Pocket009  label="case mockup top with short post holes"
  BaseFeature = -> Pad016
  Direction = (0,0,1)
  Length = 9.525
  Length2 = 5
  Profile = -> Sketch029
  ReferenceAxis = -> Sketch029 [N_Axis]
  Type = 0
FEATURE [Sketcher::SketchObject] Sketch030  label="case mockup top tall post plan"
  ExternalGeometry = -> [Pocket009]
  FullyConstrained = true
  MapMode = 5
  Placement = pos=(0,0,0) rot=(1,0,0;3.14159rad)
  Support = -> [Pocket009]
  sketch-geometry (1):
    g0: Circle CenterX=7.62 CenterY=-22.225 CenterZ=0 NormalX=0 NormalY=0 NormalZ=1 AngleXU=0 Radius=3.175
  constraints (3):
    c: DistanceY(g0,g-1) = 22.225
    c: DistanceX(g-1,g0) = 7.62
    c: Equal(g0,g-3)
FEATURE [PartDesign::Pad] Pad017  label="case mockup top with tall post"
  BaseFeature = -> Pocket009
  Direction = (0,0,-1)
  Length = 15.875
  Length2 = 10
  Profile = -> Sketch030
  ReferenceAxis = -> Sketch030 [N_Axis]
  Type = 0
FEATURE [Sketcher::SketchObject] Sketch031  label="case mockup top tall post hole plan"
  ExternalGeometry = -> [Pad017]
  FullyConstrained = true
  MapMode = 5
  Placement = pos=(0,0,-15.875) rot=(1,0,0;3.14159rad)
  Support = -> [Pad017]
  sketch-geometry (1):
    g0: Circle CenterX=7.62 CenterY=-22.225 CenterZ=0 NormalX=0 NormalY=0 NormalZ=1 AngleXU=0 Radius=1.143
  constraints (2):
    c: Coincident(g0,g-3)
    c: Equal(g0,g-4)
FEATURE [PartDesign::Pocket] Pocket010  label="case mockup top with tall post hole"
  BaseFeature = -> Pad017
  Direction = (0,0,1)
  Length = 9.525
  Length2 = 5
  Profile = -> Sketch031
  ReferenceAxis = -> Sketch031 [N_Axis]
  Type = 0
FEATURE [Sketcher::SketchObject] Sketch032  label="case mockup top tab profile"
  ExternalGeometry = -> [Pocket010]
  FullyConstrained = true
  MapMode = 5
  Placement = pos=(0,-2.54,0) rot=(1,0,0;1.5708rad)
  Support = -> [Pocket010]
  sketch-geometry (5):
    g0: LineSegment StartX=2.794 StartY=-12.065 StartZ=0 EndX=12.446 EndY=-12.065 EndZ=0
    g1: LineSegment StartX=12.446 StartY=-12.065 StartZ=0 EndX=11.43 EndY=-13.335 EndZ=0
    g2: LineSegment StartX=11.43 StartY=-13.335 StartZ=0 EndX=7.62 EndY=-13.335 EndZ=0
    g3: LineSegment StartX=7.62 StartY=-13.335 StartZ=0 EndX=3.81 EndY=-13.335 EndZ=0
    g4: LineSegment StartX=3.81 StartY=-13.335 StartZ=0 EndX=2.794 EndY=-12.065 EndZ=0
  constraints (15):
    c: Horizontal(g0)
    c: Coincident(g0,g1)
    c: Coincident(g1,g2)
    c: Horizontal(g2)
    c: Coincident(g2,g3)
    c: Horizontal(g3)
    c: Coincident(g3,g4)
    c: Coincident(g4,g0)
    c: Equal(g1,g4)
    c: Equal(g3,g2)
    c: PointOnObject(g0,g-3)
    c: DistanceY(g4,g4) = 1.27
    c: DistanceX(g2,g0) = 4.826
    c: DistanceX(g2,g2) = 3.81
    c: DistanceX(g-1,g2) = 7.62
FEATURE [PartDesign::Pad] Pad018  label="case mockup top with tab"
  BaseFeature = -> Pocket010
  Direction = (0,-1,2e-16)
  Length = 2.54
  Length2 = 10
  Profile = -> Sketch032
  ReferenceAxis = -> Sketch032 [N_Axis]
  Reversed = true
  Type = 0
FEATURE [Sketcher::SketchObject] Sketch033  label="case mockup top front hole profile"
  ExternalGeometry = -> [Pad018]
  FullyConstrained = true
  MapMode = 5
  Placement = pos=(0,-2.54,0) rot=(1,0,0;1.5708rad)
  Support = -> [Pad018]
  sketch-geometry (2):
    g0: Circle CenterX=7.62 CenterY=-13.335 CenterZ=0 NormalX=0 NormalY=0 NormalZ=1 AngleXU=0 Radius=2.794
    g1: Circle CenterX=23.495 CenterY=-12.065 CenterZ=0 NormalX=0 NormalY=0 NormalZ=1 AngleXU=0 Radius=5.08
  constraints (5):
    c: Coincident(g0,g-3)
    c: PointOnObject(g1,g-4)
    c: DistanceX(g-1,g1) = 23.495
    c: Diameter(g1) = 10.16
    c: Diameter(g0) = 5.588
FEATURE [PartDesign::Pocket] Pocket011  label="case mockup top with front holes"
  BaseFeature = -> Pad018
  Direction = (0,1,-2e-16)
  Length = 5.08
  Length2 = 5
  Profile = -> Sketch033
  ReferenceAxis = -> Sketch033 [N_Axis]
  Type = 0
FEATURE [Sketcher::SketchObject] Sketch034  label="case mockup top back wall guide plan"
  ExternalGeometry = -> [Pocket011]
  FullyConstrained = true
  MapMode = 5
  Placement = pos=(0,0,-12.065) rot=(1,0,0;3.14159rad)
  Support = -> [Pocket011]
  sketch-geometry (15):
    g0: LineSegment StartX=1.27 StartY=-62.23 StartZ=0 EndX=1.27 EndY=-63.373 EndZ=0
    g1: LineSegment StartX=1.27 StartY=-63.373 StartZ=0 EndX=0 EndY=-63.373 EndZ=0
    g2: LineSegment StartX=0 StartY=-63.373 StartZ=0 EndX=0 EndY=-64.897 EndZ=0
    g3: LineSegment StartX=0 StartY=-64.897 StartZ=0 EndX=1.27 EndY=-64.897 EndZ=0
    g4: LineSegment StartX=1.27 StartY=-64.897 StartZ=0 EndX=1.27 EndY=-66.04 EndZ=0
    g5: LineSegment StartX=1.27 StartY=-66.04 StartZ=0 EndX=30.48 EndY=-66.04 EndZ=0
    g6: LineSegment StartX=30.48 StartY=-66.04 StartZ=0 EndX=30.48 EndY=-64.897 EndZ=0
    g7: LineSegment StartX=30.48 StartY=-64.897 StartZ=0 EndX=31.75 EndY=-64.897 EndZ=0
    g8: LineSegment StartX=31.75 StartY=-64.897 StartZ=0 EndX=31.75 EndY=-63.373 EndZ=0
    g9: LineSegment StartX=31.75 StartY=-63.373 StartZ=0 EndX=30.48 EndY=-63.373 EndZ=0
    g10: LineSegment StartX=30.48 StartY=-63.373 StartZ=0 EndX=30.48 EndY=-62.23 EndZ=0
    g11: LineSegment StartX=30.48 StartY=-62.23 StartZ=0 EndX=1.27 EndY=-62.23 EndZ=0
    g12: LineSegment StartX=1.27 StartY=-64.897 StartZ=0 EndX=1.27 EndY=-63.373 EndZ=0
    g13: LineSegment StartX=30.48 StartY=-63.373 StartZ=0 EndX=30.48 EndY=-64.897 EndZ=0
    g14: LineSegment StartX=31.75 StartY=-63.373 StartZ=0 EndX=31.75 EndY=-62.23 EndZ=0
  constraints (42):
    c: Vertical(g0)
    c: Coincident(g0,g1)
    c: Horizontal(g1)
    c: Coincident(g1,g2)
    c: Vertical(g2)
    c: Coincident(g2,g3)
    c: Horizontal(g3)
    c: Coincident(g3,g4)
    c: Vertical(g4)
    c: Coincident(g4,g5)
    c: Horizontal(g5)
    c: Coincident(g5,g6)
    c: Vertical(g6)
    c: Coincident(g6,g7)
    c: Horizontal(g7)
    c: Coincident(g7,g8)
    c: Vertical(g8)
    c: Coincident(g8,g9)
    c: Horizontal(g9)
    c: Coincident(g9,g10)
    c: Vertical(g10)
    c: Coincident(g10,g11)
    c: Coincident(g11,g0)
    c: Horizontal(g11)
    c: Coincident(g12,g3)
    c: Coincident(g12,g0)
    c: Coincident(g13,g9)
    c: Coincident(g13,g6)
    c: Coincident(g14,g8)
    c: Coincident(g14,g-3)
    c: Vertical(g13)
    c: Vertical(g12)
    c: PointOnObject(g4,g-4)
    c: Vertical(g14)
    c: PointOnObject(g0,g-3)
    c: PointOnObject(g1,g-2)
    c: Equal(g3,g7)
    c: DistanceX(g2,g4) = 1.27
    c: Equal(g2,g8)
    c: DistanceY(g2,g2) = 1.524
    c: Equal(g6,g4)
    c: DistanceY(g-4,g7) = 1.143
FEATURE [PartDesign::Pocket] Pocket012  label="case mockup top with back wall guides"
  BaseFeature = -> Pocket011
  Direction = (0,0,1)
  Length = 12.065
  Length2 = 5
  Profile = -> Sketch034
  ReferenceAxis = -> Sketch034 [N_Axis]
  Type = 0
FEATURE [Sketcher::SketchObject] Sketch035  label="case mockup top back floor guide plan"
  ExternalGeometry = -> [Pocket012]
  FullyConstrained = true
  MapMode = 5
  Placement = pos=(0,0,1.8e-15) rot=(1,0,0;3.14159rad)
  Support = -> [Pocket012]
  sketch-geometry (12):
    g0: LineSegment StartX=1.27 StartY=-62.23 StartZ=0 EndX=6.35 EndY=-62.23 EndZ=0
    g1: LineSegment StartX=6.35 StartY=-62.23 StartZ=0 EndX=6.35 EndY=-63.373 EndZ=0
    g2: LineSegment StartX=6.35 StartY=-63.373 StartZ=0 EndX=1.27 EndY=-63.373 EndZ=0
    g3: LineSegment StartX=1.27 StartY=-63.373 StartZ=0 EndX=1.27 EndY=-62.23 EndZ=0
    g4: LineSegment StartX=1.27 StartY=-64.897 StartZ=0 EndX=30.48 EndY=-64.897 EndZ=0
    g5: LineSegment StartX=30.48 StartY=-64.897 StartZ=0 EndX=30.48 EndY=-66.04 EndZ=0
    g6: LineSegment StartX=30.48 StartY=-66.04 StartZ=0 EndX=1.27 EndY=-66.04 EndZ=0
    g7: LineSegment StartX=1.27 StartY=-66.04 StartZ=0 EndX=1.27 EndY=-64.897 EndZ=0
    g8: LineSegment StartX=25.4 StartY=-62.23 StartZ=0 EndX=30.48 EndY=-62.23 EndZ=0
    g9: LineSegment StartX=30.48 StartY=-62.23 StartZ=0 EndX=30.48 EndY=-63.373 EndZ=0
    g10: LineSegment StartX=30.48 StartY=-63.373 StartZ=0 EndX=25.4 EndY=-63.373 EndZ=0
    g11: LineSegment StartX=25.4 StartY=-63.373 StartZ=0 EndX=25.4 EndY=-62.23 EndZ=0
  constraints (30):
    c: Coincident(g0,g1)
    c: Coincident(g1,g2)
    c: Coincident(g2,g3)
    c: Coincident(g3,g0)
    c: Horizontal(g0)
    c: Horizontal(g2)
    c: Vertical(g1)
    c: Coincident(g4,g5)
    c: Coincident(g5,g6)
    c: Coincident(g6,g7)
    c: Coincident(g7,g4)
    c: Horizontal(g4)
    c: Horizontal(g6)
    c: Vertical(g5)
    c: Vertical(g7)
    c: Coincident(g8,g9)
    c: Coincident(g9,g10)
    c: Coincident(g10,g11)
    c: Coincident(g11,g8)
    c: Horizontal(g8)
    c: Horizontal(g10)
    c: Vertical(g11)
    c: Coincident(g8,g-5)
    c: Coincident(g9,g-5)
    c: Coincident(g0,g-6)
    c: Coincident(g2,g-6)
    c: Coincident(g4,g-3)
    c: Coincident(g5,g-4)
    c: Equal(g0,g8)
    c: DistanceX(g0,g0) = 5.08
FEATURE [PartDesign::Pad] Pad019  label="case mockup top with back floor guide"
  BaseFeature = -> Pocket012
  Direction = (0,0,-1)
  Length = 1.27
  Length2 = 10
  Profile = -> Sketch035
  ReferenceAxis = -> Sketch035 [N_Axis]
  Type = 0
FEATURE [Sketcher::SketchObject] Sketch036  label="case mockup top trench plan"
  ExternalGeometry = -> [Pad019]
  FullyConstrained = true
  MapMode = 5
  Placement = pos=(0,0,-12.065) rot=(1,0,0;3.14159rad)
  Support = -> [Pad019]
  sketch-geometry (16):
    g0: LineSegment StartX=-1.397 StartY=1.397 StartZ=0 EndX=-1.397 EndY=-63.627 EndZ=0
    g1: LineSegment StartX=-1.397 StartY=-63.627 StartZ=0 EndX=33.147 EndY=-63.627 EndZ=0
    g2: LineSegment StartX=33.147 StartY=-63.627 StartZ=0 EndX=33.147 EndY=1.397 EndZ=0
    g3: LineSegment StartX=33.147 StartY=1.397 StartZ=0 EndX=12.446 EndY=1.397 EndZ=0
    g4: LineSegment StartX=12.446 StartY=1.397 StartZ=0 EndX=12.446 EndY=8.9e-15 EndZ=0
    g5: LineSegment StartX=12.446 StartY=8.9e-15 StartZ=0 EndX=31.75 EndY=8.9e-15 EndZ=0
    g6: LineSegment StartX=31.75 StartY=8.9e-15 StartZ=0 EndX=31.75 EndY=-62.23 EndZ=0
    g7: LineSegment StartX=31.75 StartY=-62.23 StartZ=0 EndX=0 EndY=-62.23 EndZ=0
    g8: LineSegment StartX=0 StartY=-62.23 StartZ=0 EndX=0 EndY=7.1e-15 EndZ=0
    g9: LineSegment StartX=0 StartY=7.1e-15 StartZ=0 EndX=2.794 EndY=7.1e-15 EndZ=0
    g10: LineSegment StartX=2.794 StartY=7.1e-15 StartZ=0 EndX=2.794 EndY=1.397 EndZ=0
    g11: LineSegment StartX=2.794 StartY=1.397 StartZ=0 EndX=-1.397 EndY=1.397 EndZ=0
    g12: LineSegment StartX=2.794 StartY=1.397 StartZ=0 EndX=12.446 EndY=1.397 EndZ=0
    g13: LineSegment StartX=31.75 StartY=8.9e-15 StartZ=0 EndX=33.147 EndY=8.9e-15 EndZ=0
    g14: LineSegment StartX=0 StartY=-62.23 StartZ=0 EndX=-1.397 EndY=-62.23 EndZ=0
    g15: LineSegment StartX=31.75 StartY=-62.23 StartZ=0 EndX=31.75 EndY=-63.627 EndZ=0
  constraints (43):
    c: Vertical(g0)
    c: Coincident(g0,g1)
    c: Horizontal(g1)
    c: Coincident(g1,g2)
    c: Vertical(g2)
    c: Coincident(g2,g3)
    c: Horizontal(g3)
    c: Coincident(g3,g4)
    c: Vertical(g4)
    c: Coincident(g4,g5)
    c: Horizontal(g5)
    c: Coincident(g5,g6)
    c: Vertical(g6)
    c: Coincident(g6,g7)
    c: Coincident(g7,g8)
    c: Vertical(g8)
    c: Coincident(g8,g9)
    c: Horizontal(g9)
    c: Coincident(g9,g10)
    c: Vertical(g10)
    c: Coincident(g10,g11)
    c: Coincident(g11,g0)
    c: Horizontal(g11)
    c: Coincident(g9,g-3)
    c: Coincident(g4,g-4)
    c: Coincident(g7,g-6)
    c: Coincident(g6,g-5)
    c: Coincident(g12,g10)
    c: Coincident(g12,g3)
    c: Horizontal(g12)
    c: Coincident(g13,g5)
    c: PointOnObject(g13,g2)
    c: Horizontal(g13)
    c: Coincident(g14,g7)
    c: PointOnObject(g14,g0)
    c: Horizontal(g14)
    c: Coincident(g15,g6)
    c: PointOnObject(g15,g1)
    c: Vertical(g15)
    c: Equal(g15,g14)
    c: Equal(g14,g13)
    c: Equal(g4,g13)
    c: DistanceX(g5,g2) = 1.397
FEATURE [PartDesign::Pocket] Pocket013  label="case mockup top with trench"
  BaseFeature = -> Pad019
  Direction = (0,0,1)
  Length = 1.524
  Length2 = 5
  Profile = -> Sketch036
  ReferenceAxis = -> Sketch036 [N_Axis]
  Type = 0
FEATURE [App::DocumentObjectGroup] Group006  label="mounting screws for mockup"
  Group = -> [Body013,Body014,Body015,Body016]
FEATURE [App::DocumentObjectGroup] Group007  label="case screws for mockup"
  Group = -> [Body009,Body010,Body011]
FEATURE [PartDesign::Fillet] Fillet  label="case mockup top with external round"
  Base = -> Pocket013 [Edge10,Edge20,Edge7,Edge4,Edge2,Edge11,Edge8,Edge26,Edge24,Edge5,Edge19,Edge1]
  BaseFeature = -> Pocket013
  Radius = 1.27
  SupportTransform = false
  UseAllEdges = false
FEATURE [PartDesign::Body] Body019  label="case mockup top body"
  Group = -> [Sketch026,Pad014,Sketch027,Pad015,Sketch028,Pad016,Sketch029,Pocket009,Sketch030,Pad017,Sketch031,Pocket010,Sketch032,Pad018,Sketch033,Pocket011,Sketch034,Pocket012,Sketch035,Pad019,Sketch036,Pocket013,Fillet]
  Origin = -> Origin019
  Tip = -> Fillet
FEATURE [PartDesign::FeatureBase] Clone013
  BaseFeature = -> Body019
FEATURE [PartDesign::Body] Body020  label="case mockup top clone"
  Group = -> [Clone013]
  Origin = -> Origin020
  Placement = pos=(0,0,15.875) rot=(0,0,1;0rad)
  Tip = -> Clone013
FEATURE [PartDesign::Fillet] Fillet001  label="case mockup bottom ears with vertical rounds"
  Base = -> Pad012 [Edge35,Edge6,Edge37,Edge109,Edge11,Edge9,Edge47,Edge51]
  BaseFeature = -> Pad012
  Radius = 1.27
  SupportTransform = false
  UseAllEdges = false
FEATURE [PartDesign::Fillet] Fillet002  label="case mockup bottom ears with slot rounds"
  Base = -> Fillet001 [Edge345,Edge206,Edge343,Edge201,Edge344,Edge204,Edge342,Edge202,Edge76,Edge75,Edge74,Edge73,Edge37,Edge38,Edge266,Edge139,Edge265,Edge267,Edge261,Edge260,Edge134,Edge35,Edge36,Edge264,Edge137,Edge263,Edge262,Edge135,Edge336,Edge335,Edge338,Edge337]
  BaseFeature = -> Fillet001
  Radius = 0.762
  SupportTransform = false
  UseAllEdges = false
FEATURE [PartDesign::Fillet] Fillet003  label="case mockup bottom ears with ear rounds"
  Base = -> Fillet002 [Edge61,Edge63,Edge71,Edge173,Edge241,Edge243,Edge244,Edge133,Edge52,Edge55,Edge57,Edge59,Edge73,Edge125,Edge126,Edge127,Edge128,Edge17,Edge16,Edge15,Edge14,Edge13,Edge12,Edge11,Edge50,Edge129,Edge130,Edge131,Edge19,Edge20]
  BaseFeature = -> Fillet002
  Radius = 0.762
  SupportTransform = false
  UseAllEdges = false
FEATURE [PartDesign::Body] Body006  label="case mockup bottom ears body"
  BaseFeature = -> Body004
  Group = -> [Clone003,Sketch020,Pad011,Sketch021,Pad012,Fillet001,Fillet002,Fillet003]
  Origin = -> Origin006
  Tip = -> Fillet003
FEATURE [PartDesign::FeatureBase] Clone004
  BaseFeature = -> Body006
FEATURE [PartDesign::Body] Body007  label="case mockup bottom clone with ears"
  BaseFeature = -> Body006
  Group = -> [Clone004]
  Origin = -> Origin007
  Tip = -> Clone004
FEATURE [PartDesign::FeatureBase] Clone014
  BaseFeature = -> Body004
FEATURE [PartDesign::Fillet] Fillet004  label="case mockup bottom rounded with edge rounds"
  Base = -> Clone014 [Edge9,Edge8,Edge6,Edge33,Edge102,Edge34,Edge7,Edge36,Edge37,Edge38,Edge44,Edge42]
  BaseFeature = -> Clone014
  Radius = 1.27
  SupportTransform = false
  UseAllEdges = false
FEATURE [PartDesign::Fillet] Fillet005  label="case mockup bottom rounded with hole rounds"
  Base = -> Fillet004 [Edge84,Edge86,Edge85]
  BaseFeature = -> Fillet004
  Radius = 0.762
  SupportTransform = false
  UseAllEdges = false
FEATURE [PartDesign::Body] Body021  label="case mockup bottom rounded body"
  Group = -> [Clone014,Fillet004,Fillet005]
  Origin = -> Origin021
  Tip = -> Fillet005
FEATURE [App::DocumentObjectGroup] Group002  label="case mockup parts"
  Group = -> [Body004,Body006,Body017,Body019,Body021]
FEATURE [PartDesign::FeatureBase] Clone002
  BaseFeature = -> Body021
FEATURE [PartDesign::Body] Body005  label="case mockup bottom clone no ears"
  BaseFeature = -> Body021
  Group = -> [Clone002]
  Origin = -> Origin005
  Tip = -> Clone002
FEATURE [App::DocumentObjectGroup] Group003  label="mockups"
  Group = -> [Body002,Body003,Body005,Body007,Body018,Body020,Group006,Group007]
FEATURE [Mesh::Feature] Mesh  label="case mockup bottom ears mesh"
FEATURE [Mesh::Feature] Mesh001  label="case mockup bottom plain mesh"
FEATURE [Mesh::Feature] Mesh002  label="case mockup top mesh"
FEATURE [Mesh::Feature] Mesh003  label="case mockup plate mesh"
FEATURE [App::DocumentObjectGroup] Group  label="meshes"
  Group = -> [Mesh,Mesh001,Mesh002,Mesh003]
